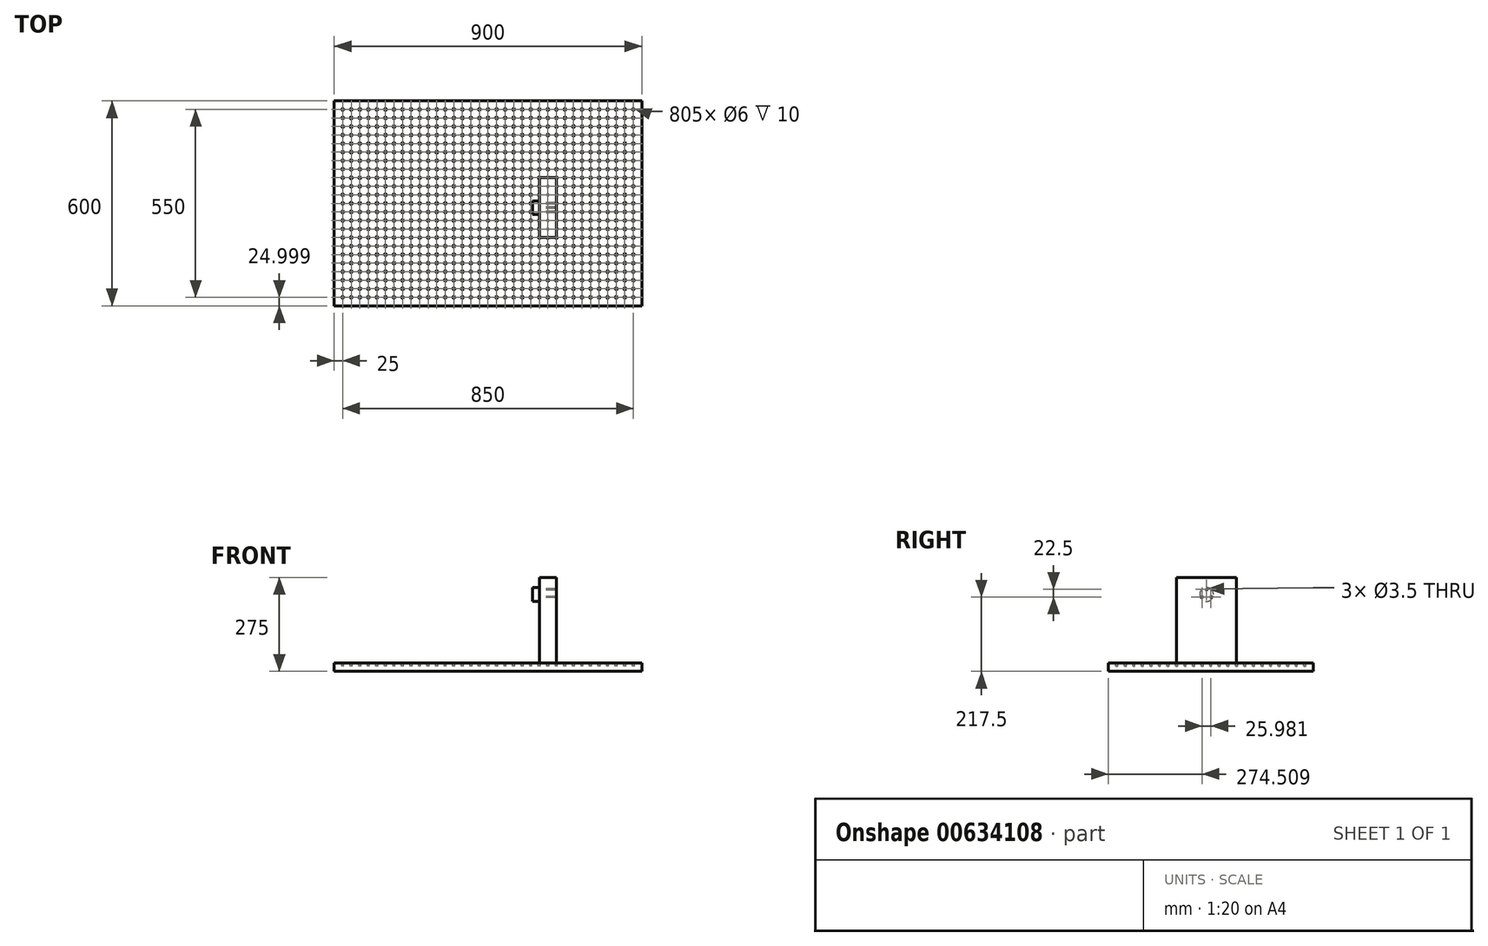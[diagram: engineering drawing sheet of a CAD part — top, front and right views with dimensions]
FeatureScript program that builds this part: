
annotation { "Feature Type Name" : "Feature", "Feature Type Description" : "" }
export const myFeature = defineFeature(function(context is Context, id is Id, definition is map)
    precondition{}
    {
        {
            var Q0;
            Q0=qCreatedBy(makeId("Top.planeOp"),FACE);
            var sketch = newSketch(context, id + "F0", { "sketchPlane" : qUnion([Q0])});
            skLineSegment(sketch, "E0.bottom", {"start": v(0, 7.98) * mm, "end": v(900, 7.98) * mm});
            skLineSegment(sketch, "E0.top", {"start": v(0, 607.98) * mm, "end": v(900, 607.98) * mm});
            skLineSegment(sketch, "E0.left", {"start": v(0, 7.98) * mm, "end": v(0, 607.98) * mm});
            skLineSegment(sketch, "E0.right", {"start": v(900, 7.98) * mm, "end": v(900, 607.98) * mm});
            skSolve(sketch);
        }
        {
            var Q0;
            Q0=makeQuery(id+"F0.imprint","IMPRINT",FACE,{"disambiguationData":[TD([[makeQuery(id+"F0.imprint","IMPRINT",EDGE,{"derivedFrom":sQuery(id+"F0.wireOp",EDGE,"E0.bottom")}),1.0]])]});
            extrude(context, id + "F1", {"entities" : qUnion([Q0]), "depth" : 25 * mm});
        }
        {
            var Q0;
            Q0=makeQuery(id+"F1.opExtrude","CAP_FACE",FACE,{"disambiguationData":[OSD([sQuery(id+"F0.wireOp",EDGE,"E0.bottom"),sQuery(id+"F0.wireOp",EDGE,"E0.top"),sQuery(id+"F0.wireOp",EDGE,"E0.left"),sQuery(id+"F0.wireOp",EDGE,"E0.right")])],"isStart":false});
            var sketch = newSketch(context, id + "F2", { "sketchPlane" : qUnion([Q0])});
            skCircle(sketch, "E1", {"center": v(25, 32.98) * mm, "radius": 3 * mm});
            skCircle(sketch, "E2.0.1.0", {"center": v(25, 57.98) * mm, "radius": 3 * mm});
            skCircle(sketch, "E2.0.2.0", {"center": v(25, 82.98) * mm, "radius": 3 * mm});
            skCircle(sketch, "E2.0.3.0", {"center": v(25, 107.98) * mm, "radius": 3 * mm});
            skCircle(sketch, "E2.0.4.0", {"center": v(25, 132.98) * mm, "radius": 3 * mm});
            skCircle(sketch, "E2.0.5.0", {"center": v(25, 157.98) * mm, "radius": 3 * mm});
            skCircle(sketch, "E2.0.6.0", {"center": v(25, 182.98) * mm, "radius": 3 * mm});
            skCircle(sketch, "E2.0.7.0", {"center": v(25, 207.98) * mm, "radius": 3 * mm});
            skCircle(sketch, "E2.0.8.0", {"center": v(25, 232.98) * mm, "radius": 3 * mm});
            skCircle(sketch, "E2.0.9.0", {"center": v(25, 257.98) * mm, "radius": 3 * mm});
            skCircle(sketch, "E2.0.10.0", {"center": v(25, 282.98) * mm, "radius": 3 * mm});
            skCircle(sketch, "E2.0.11.0", {"center": v(25, 307.98) * mm, "radius": 3 * mm});
            skCircle(sketch, "E2.0.12.0", {"center": v(25, 332.98) * mm, "radius": 3 * mm});
            skCircle(sketch, "E2.0.13.0", {"center": v(25, 357.98) * mm, "radius": 3 * mm});
            skCircle(sketch, "E2.0.14.0", {"center": v(25, 382.98) * mm, "radius": 3 * mm});
            skCircle(sketch, "E2.0.15.0", {"center": v(25, 407.98) * mm, "radius": 3 * mm});
            skCircle(sketch, "E2.0.16.0", {"center": v(25, 432.98) * mm, "radius": 3 * mm});
            skCircle(sketch, "E2.0.17.0", {"center": v(25, 457.98) * mm, "radius": 3 * mm});
            skCircle(sketch, "E2.0.18.0", {"center": v(25, 482.98) * mm, "radius": 3 * mm});
            skCircle(sketch, "E2.0.19.0", {"center": v(25, 507.98) * mm, "radius": 3 * mm});
            skCircle(sketch, "E2.0.20.0", {"center": v(25, 532.98) * mm, "radius": 3 * mm});
            skCircle(sketch, "E2.0.21.0", {"center": v(25, 557.98) * mm, "radius": 3 * mm});
            skCircle(sketch, "E2.0.22.0", {"center": v(25, 582.98) * mm, "radius": 3 * mm});
            skCircle(sketch, "E2.1.0.0", {"center": v(50, 32.98) * mm, "radius": 3 * mm});
            skCircle(sketch, "E2.1.1.0", {"center": v(50, 57.98) * mm, "radius": 3 * mm});
            skCircle(sketch, "E2.1.2.0", {"center": v(50, 82.98) * mm, "radius": 3 * mm});
            skCircle(sketch, "E2.1.3.0", {"center": v(50, 107.98) * mm, "radius": 3 * mm});
            skCircle(sketch, "E2.1.4.0", {"center": v(50, 132.98) * mm, "radius": 3 * mm});
            skCircle(sketch, "E2.1.5.0", {"center": v(50, 157.98) * mm, "radius": 3 * mm});
            skCircle(sketch, "E2.1.6.0", {"center": v(50, 182.98) * mm, "radius": 3 * mm});
            skCircle(sketch, "E2.1.7.0", {"center": v(50, 207.98) * mm, "radius": 3 * mm});
            skCircle(sketch, "E2.1.8.0", {"center": v(50, 232.98) * mm, "radius": 3 * mm});
            skCircle(sketch, "E2.1.9.0", {"center": v(50, 257.98) * mm, "radius": 3 * mm});
            skCircle(sketch, "E2.1.10.0", {"center": v(50, 282.98) * mm, "radius": 3 * mm});
            skCircle(sketch, "E2.1.11.0", {"center": v(50, 307.98) * mm, "radius": 3 * mm});
            skCircle(sketch, "E2.1.12.0", {"center": v(50, 332.98) * mm, "radius": 3 * mm});
            skCircle(sketch, "E2.1.13.0", {"center": v(50, 357.98) * mm, "radius": 3 * mm});
            skCircle(sketch, "E2.1.14.0", {"center": v(50, 382.98) * mm, "radius": 3 * mm});
            skCircle(sketch, "E2.1.15.0", {"center": v(50, 407.98) * mm, "radius": 3 * mm});
            skCircle(sketch, "E2.1.16.0", {"center": v(50, 432.98) * mm, "radius": 3 * mm});
            skCircle(sketch, "E2.1.17.0", {"center": v(50, 457.98) * mm, "radius": 3 * mm});
            skCircle(sketch, "E2.1.18.0", {"center": v(50, 482.98) * mm, "radius": 3 * mm});
            skCircle(sketch, "E2.1.19.0", {"center": v(50, 507.98) * mm, "radius": 3 * mm});
            skCircle(sketch, "E2.1.20.0", {"center": v(50, 532.98) * mm, "radius": 3 * mm});
            skCircle(sketch, "E2.1.21.0", {"center": v(50, 557.98) * mm, "radius": 3 * mm});
            skCircle(sketch, "E2.1.22.0", {"center": v(50, 582.98) * mm, "radius": 3 * mm});
            skCircle(sketch, "E2.2.0.0", {"center": v(75, 32.98) * mm, "radius": 3 * mm});
            skCircle(sketch, "E2.2.1.0", {"center": v(75, 57.98) * mm, "radius": 3 * mm});
            skCircle(sketch, "E2.2.2.0", {"center": v(75, 82.98) * mm, "radius": 3 * mm});
            skCircle(sketch, "E2.2.3.0", {"center": v(75, 107.98) * mm, "radius": 3 * mm});
            skCircle(sketch, "E2.2.4.0", {"center": v(75, 132.98) * mm, "radius": 3 * mm});
            skCircle(sketch, "E2.2.5.0", {"center": v(75, 157.98) * mm, "radius": 3 * mm});
            skCircle(sketch, "E2.2.6.0", {"center": v(75, 182.98) * mm, "radius": 3 * mm});
            skCircle(sketch, "E2.2.7.0", {"center": v(75, 207.98) * mm, "radius": 3 * mm});
            skCircle(sketch, "E2.2.8.0", {"center": v(75, 232.98) * mm, "radius": 3 * mm});
            skCircle(sketch, "E2.2.9.0", {"center": v(75, 257.98) * mm, "radius": 3 * mm});
            skCircle(sketch, "E2.2.10.0", {"center": v(75, 282.98) * mm, "radius": 3 * mm});
            skCircle(sketch, "E2.2.11.0", {"center": v(75, 307.98) * mm, "radius": 3 * mm});
            skCircle(sketch, "E2.2.12.0", {"center": v(75, 332.98) * mm, "radius": 3 * mm});
            skCircle(sketch, "E2.2.13.0", {"center": v(75, 357.98) * mm, "radius": 3 * mm});
            skCircle(sketch, "E2.2.14.0", {"center": v(75, 382.98) * mm, "radius": 3 * mm});
            skCircle(sketch, "E2.2.15.0", {"center": v(75, 407.98) * mm, "radius": 3 * mm});
            skCircle(sketch, "E2.2.16.0", {"center": v(75, 432.98) * mm, "radius": 3 * mm});
            skCircle(sketch, "E2.2.17.0", {"center": v(75, 457.98) * mm, "radius": 3 * mm});
            skCircle(sketch, "E2.2.18.0", {"center": v(75, 482.98) * mm, "radius": 3 * mm});
            skCircle(sketch, "E2.2.19.0", {"center": v(75, 507.98) * mm, "radius": 3 * mm});
            skCircle(sketch, "E2.2.20.0", {"center": v(75, 532.98) * mm, "radius": 3 * mm});
            skCircle(sketch, "E2.2.21.0", {"center": v(75, 557.98) * mm, "radius": 3 * mm});
            skCircle(sketch, "E2.2.22.0", {"center": v(75, 582.98) * mm, "radius": 3 * mm});
            skCircle(sketch, "E2.3.0.0", {"center": v(100, 32.98) * mm, "radius": 3 * mm});
            skCircle(sketch, "E2.3.1.0", {"center": v(100, 57.98) * mm, "radius": 3 * mm});
            skCircle(sketch, "E2.3.2.0", {"center": v(100, 82.98) * mm, "radius": 3 * mm});
            skCircle(sketch, "E2.3.3.0", {"center": v(100, 107.98) * mm, "radius": 3 * mm});
            skCircle(sketch, "E2.3.4.0", {"center": v(100, 132.98) * mm, "radius": 3 * mm});
            skCircle(sketch, "E2.3.5.0", {"center": v(100, 157.98) * mm, "radius": 3 * mm});
            skCircle(sketch, "E2.3.6.0", {"center": v(100, 182.98) * mm, "radius": 3 * mm});
            skCircle(sketch, "E2.3.7.0", {"center": v(100, 207.98) * mm, "radius": 3 * mm});
            skCircle(sketch, "E2.3.8.0", {"center": v(100, 232.98) * mm, "radius": 3 * mm});
            skCircle(sketch, "E2.3.9.0", {"center": v(100, 257.98) * mm, "radius": 3 * mm});
            skCircle(sketch, "E2.3.10.0", {"center": v(100, 282.98) * mm, "radius": 3 * mm});
            skCircle(sketch, "E2.3.11.0", {"center": v(100, 307.98) * mm, "radius": 3 * mm});
            skCircle(sketch, "E2.3.12.0", {"center": v(100, 332.98) * mm, "radius": 3 * mm});
            skCircle(sketch, "E2.3.13.0", {"center": v(100, 357.98) * mm, "radius": 3 * mm});
            skCircle(sketch, "E2.3.14.0", {"center": v(100, 382.98) * mm, "radius": 3 * mm});
            skCircle(sketch, "E2.3.15.0", {"center": v(100, 407.98) * mm, "radius": 3 * mm});
            skCircle(sketch, "E2.3.16.0", {"center": v(100, 432.98) * mm, "radius": 3 * mm});
            skCircle(sketch, "E2.3.17.0", {"center": v(100, 457.98) * mm, "radius": 3 * mm});
            skCircle(sketch, "E2.3.18.0", {"center": v(100, 482.98) * mm, "radius": 3 * mm});
            skCircle(sketch, "E2.3.19.0", {"center": v(100, 507.98) * mm, "radius": 3 * mm});
            skCircle(sketch, "E2.3.20.0", {"center": v(100, 532.98) * mm, "radius": 3 * mm});
            skCircle(sketch, "E2.3.21.0", {"center": v(100, 557.98) * mm, "radius": 3 * mm});
            skCircle(sketch, "E2.3.22.0", {"center": v(100, 582.98) * mm, "radius": 3 * mm});
            skCircle(sketch, "E2.4.0.0", {"center": v(125, 32.98) * mm, "radius": 3 * mm});
            skCircle(sketch, "E2.4.1.0", {"center": v(125, 57.98) * mm, "radius": 3 * mm});
            skCircle(sketch, "E2.4.2.0", {"center": v(125, 82.98) * mm, "radius": 3 * mm});
            skCircle(sketch, "E2.4.3.0", {"center": v(125, 107.98) * mm, "radius": 3 * mm});
            skCircle(sketch, "E2.4.4.0", {"center": v(125, 132.98) * mm, "radius": 3 * mm});
            skCircle(sketch, "E2.4.5.0", {"center": v(125, 157.98) * mm, "radius": 3 * mm});
            skCircle(sketch, "E2.4.6.0", {"center": v(125, 182.98) * mm, "radius": 3 * mm});
            skCircle(sketch, "E2.4.7.0", {"center": v(125, 207.98) * mm, "radius": 3 * mm});
            skCircle(sketch, "E2.4.8.0", {"center": v(125, 232.98) * mm, "radius": 3 * mm});
            skCircle(sketch, "E2.4.9.0", {"center": v(125, 257.98) * mm, "radius": 3 * mm});
            skCircle(sketch, "E2.4.10.0", {"center": v(125, 282.98) * mm, "radius": 3 * mm});
            skCircle(sketch, "E2.4.11.0", {"center": v(125, 307.98) * mm, "radius": 3 * mm});
            skCircle(sketch, "E2.4.12.0", {"center": v(125, 332.98) * mm, "radius": 3 * mm});
            skCircle(sketch, "E2.4.13.0", {"center": v(125, 357.98) * mm, "radius": 3 * mm});
            skCircle(sketch, "E2.4.14.0", {"center": v(125, 382.98) * mm, "radius": 3 * mm});
            skCircle(sketch, "E2.4.15.0", {"center": v(125, 407.98) * mm, "radius": 3 * mm});
            skCircle(sketch, "E2.4.16.0", {"center": v(125, 432.98) * mm, "radius": 3 * mm});
            skCircle(sketch, "E2.4.17.0", {"center": v(125, 457.98) * mm, "radius": 3 * mm});
            skCircle(sketch, "E2.4.18.0", {"center": v(125, 482.98) * mm, "radius": 3 * mm});
            skCircle(sketch, "E2.4.19.0", {"center": v(125, 507.98) * mm, "radius": 3 * mm});
            skCircle(sketch, "E2.4.20.0", {"center": v(125, 532.98) * mm, "radius": 3 * mm});
            skCircle(sketch, "E2.4.21.0", {"center": v(125, 557.98) * mm, "radius": 3 * mm});
            skCircle(sketch, "E2.4.22.0", {"center": v(125, 582.98) * mm, "radius": 3 * mm});
            skCircle(sketch, "E2.5.0.0", {"center": v(150, 32.98) * mm, "radius": 3 * mm});
            skCircle(sketch, "E2.5.1.0", {"center": v(150, 57.98) * mm, "radius": 3 * mm});
            skCircle(sketch, "E2.5.2.0", {"center": v(150, 82.98) * mm, "radius": 3 * mm});
            skCircle(sketch, "E2.5.3.0", {"center": v(150, 107.98) * mm, "radius": 3 * mm});
            skCircle(sketch, "E2.5.4.0", {"center": v(150, 132.98) * mm, "radius": 3 * mm});
            skCircle(sketch, "E2.5.5.0", {"center": v(150, 157.98) * mm, "radius": 3 * mm});
            skCircle(sketch, "E2.5.6.0", {"center": v(150, 182.98) * mm, "radius": 3 * mm});
            skCircle(sketch, "E2.5.7.0", {"center": v(150, 207.98) * mm, "radius": 3 * mm});
            skCircle(sketch, "E2.5.8.0", {"center": v(150, 232.98) * mm, "radius": 3 * mm});
            skCircle(sketch, "E2.5.9.0", {"center": v(150, 257.98) * mm, "radius": 3 * mm});
            skCircle(sketch, "E2.5.10.0", {"center": v(150, 282.98) * mm, "radius": 3 * mm});
            skCircle(sketch, "E2.5.11.0", {"center": v(150, 307.98) * mm, "radius": 3 * mm});
            skCircle(sketch, "E2.5.12.0", {"center": v(150, 332.98) * mm, "radius": 3 * mm});
            skCircle(sketch, "E2.5.13.0", {"center": v(150, 357.98) * mm, "radius": 3 * mm});
            skCircle(sketch, "E2.5.14.0", {"center": v(150, 382.98) * mm, "radius": 3 * mm});
            skCircle(sketch, "E2.5.15.0", {"center": v(150, 407.98) * mm, "radius": 3 * mm});
            skCircle(sketch, "E2.5.16.0", {"center": v(150, 432.98) * mm, "radius": 3 * mm});
            skCircle(sketch, "E2.5.17.0", {"center": v(150, 457.98) * mm, "radius": 3 * mm});
            skCircle(sketch, "E2.5.18.0", {"center": v(150, 482.98) * mm, "radius": 3 * mm});
            skCircle(sketch, "E2.5.19.0", {"center": v(150, 507.98) * mm, "radius": 3 * mm});
            skCircle(sketch, "E2.5.20.0", {"center": v(150, 532.98) * mm, "radius": 3 * mm});
            skCircle(sketch, "E2.5.21.0", {"center": v(150, 557.98) * mm, "radius": 3 * mm});
            skCircle(sketch, "E2.5.22.0", {"center": v(150, 582.98) * mm, "radius": 3 * mm});
            skCircle(sketch, "E2.6.0.0", {"center": v(175, 32.98) * mm, "radius": 3 * mm});
            skCircle(sketch, "E2.6.1.0", {"center": v(175, 57.98) * mm, "radius": 3 * mm});
            skCircle(sketch, "E2.6.2.0", {"center": v(175, 82.98) * mm, "radius": 3 * mm});
            skCircle(sketch, "E2.6.3.0", {"center": v(175, 107.98) * mm, "radius": 3 * mm});
            skCircle(sketch, "E2.6.4.0", {"center": v(175, 132.98) * mm, "radius": 3 * mm});
            skCircle(sketch, "E2.6.5.0", {"center": v(175, 157.98) * mm, "radius": 3 * mm});
            skCircle(sketch, "E2.6.6.0", {"center": v(175, 182.98) * mm, "radius": 3 * mm});
            skCircle(sketch, "E2.6.7.0", {"center": v(175, 207.98) * mm, "radius": 3 * mm});
            skCircle(sketch, "E2.6.8.0", {"center": v(175, 232.98) * mm, "radius": 3 * mm});
            skCircle(sketch, "E2.6.9.0", {"center": v(175, 257.98) * mm, "radius": 3 * mm});
            skCircle(sketch, "E2.6.10.0", {"center": v(175, 282.98) * mm, "radius": 3 * mm});
            skCircle(sketch, "E2.6.11.0", {"center": v(175, 307.98) * mm, "radius": 3 * mm});
            skCircle(sketch, "E2.6.12.0", {"center": v(175, 332.98) * mm, "radius": 3 * mm});
            skCircle(sketch, "E2.6.13.0", {"center": v(175, 357.98) * mm, "radius": 3 * mm});
            skCircle(sketch, "E2.6.14.0", {"center": v(175, 382.98) * mm, "radius": 3 * mm});
            skCircle(sketch, "E2.6.15.0", {"center": v(175, 407.98) * mm, "radius": 3 * mm});
            skCircle(sketch, "E2.6.16.0", {"center": v(175, 432.98) * mm, "radius": 3 * mm});
            skCircle(sketch, "E2.6.17.0", {"center": v(175, 457.98) * mm, "radius": 3 * mm});
            skCircle(sketch, "E2.6.18.0", {"center": v(175, 482.98) * mm, "radius": 3 * mm});
            skCircle(sketch, "E2.6.19.0", {"center": v(175, 507.98) * mm, "radius": 3 * mm});
            skCircle(sketch, "E2.6.20.0", {"center": v(175, 532.98) * mm, "radius": 3 * mm});
            skCircle(sketch, "E2.6.21.0", {"center": v(175, 557.98) * mm, "radius": 3 * mm});
            skCircle(sketch, "E2.6.22.0", {"center": v(175, 582.98) * mm, "radius": 3 * mm});
            skCircle(sketch, "E2.7.0.0", {"center": v(200, 32.98) * mm, "radius": 3 * mm});
            skCircle(sketch, "E2.7.1.0", {"center": v(200, 57.98) * mm, "radius": 3 * mm});
            skCircle(sketch, "E2.7.2.0", {"center": v(200, 82.98) * mm, "radius": 3 * mm});
            skCircle(sketch, "E2.7.3.0", {"center": v(200, 107.98) * mm, "radius": 3 * mm});
            skCircle(sketch, "E2.7.4.0", {"center": v(200, 132.98) * mm, "radius": 3 * mm});
            skCircle(sketch, "E2.7.5.0", {"center": v(200, 157.98) * mm, "radius": 3 * mm});
            skCircle(sketch, "E2.7.6.0", {"center": v(200, 182.98) * mm, "radius": 3 * mm});
            skCircle(sketch, "E2.7.7.0", {"center": v(200, 207.98) * mm, "radius": 3 * mm});
            skCircle(sketch, "E2.7.8.0", {"center": v(200, 232.98) * mm, "radius": 3 * mm});
            skCircle(sketch, "E2.7.9.0", {"center": v(200, 257.98) * mm, "radius": 3 * mm});
            skCircle(sketch, "E2.7.10.0", {"center": v(200, 282.98) * mm, "radius": 3 * mm});
            skCircle(sketch, "E2.7.11.0", {"center": v(200, 307.98) * mm, "radius": 3 * mm});
            skCircle(sketch, "E2.7.12.0", {"center": v(200, 332.98) * mm, "radius": 3 * mm});
            skCircle(sketch, "E2.7.13.0", {"center": v(200, 357.98) * mm, "radius": 3 * mm});
            skCircle(sketch, "E2.7.14.0", {"center": v(200, 382.98) * mm, "radius": 3 * mm});
            skCircle(sketch, "E2.7.15.0", {"center": v(200, 407.98) * mm, "radius": 3 * mm});
            skCircle(sketch, "E2.7.16.0", {"center": v(200, 432.98) * mm, "radius": 3 * mm});
            skCircle(sketch, "E2.7.17.0", {"center": v(200, 457.98) * mm, "radius": 3 * mm});
            skCircle(sketch, "E2.7.18.0", {"center": v(200, 482.98) * mm, "radius": 3 * mm});
            skCircle(sketch, "E2.7.19.0", {"center": v(200, 507.98) * mm, "radius": 3 * mm});
            skCircle(sketch, "E2.7.20.0", {"center": v(200, 532.98) * mm, "radius": 3 * mm});
            skCircle(sketch, "E2.7.21.0", {"center": v(200, 557.98) * mm, "radius": 3 * mm});
            skCircle(sketch, "E2.7.22.0", {"center": v(200, 582.98) * mm, "radius": 3 * mm});
            skCircle(sketch, "E2.8.0.0", {"center": v(225, 32.98) * mm, "radius": 3 * mm});
            skCircle(sketch, "E2.8.1.0", {"center": v(225, 57.98) * mm, "radius": 3 * mm});
            skCircle(sketch, "E2.8.2.0", {"center": v(225, 82.98) * mm, "radius": 3 * mm});
            skCircle(sketch, "E2.8.3.0", {"center": v(225, 107.98) * mm, "radius": 3 * mm});
            skCircle(sketch, "E2.8.4.0", {"center": v(225, 132.98) * mm, "radius": 3 * mm});
            skCircle(sketch, "E2.8.5.0", {"center": v(225, 157.98) * mm, "radius": 3 * mm});
            skCircle(sketch, "E2.8.6.0", {"center": v(225, 182.98) * mm, "radius": 3 * mm});
            skCircle(sketch, "E2.8.7.0", {"center": v(225, 207.98) * mm, "radius": 3 * mm});
            skCircle(sketch, "E2.8.8.0", {"center": v(225, 232.98) * mm, "radius": 3 * mm});
            skCircle(sketch, "E2.8.9.0", {"center": v(225, 257.98) * mm, "radius": 3 * mm});
            skCircle(sketch, "E2.8.10.0", {"center": v(225, 282.98) * mm, "radius": 3 * mm});
            skCircle(sketch, "E2.8.11.0", {"center": v(225, 307.98) * mm, "radius": 3 * mm});
            skCircle(sketch, "E2.8.12.0", {"center": v(225, 332.98) * mm, "radius": 3 * mm});
            skCircle(sketch, "E2.8.13.0", {"center": v(225, 357.98) * mm, "radius": 3 * mm});
            skCircle(sketch, "E2.8.14.0", {"center": v(225, 382.98) * mm, "radius": 3 * mm});
            skCircle(sketch, "E2.8.15.0", {"center": v(225, 407.98) * mm, "radius": 3 * mm});
            skCircle(sketch, "E2.8.16.0", {"center": v(225, 432.98) * mm, "radius": 3 * mm});
            skCircle(sketch, "E2.8.17.0", {"center": v(225, 457.98) * mm, "radius": 3 * mm});
            skCircle(sketch, "E2.8.18.0", {"center": v(225, 482.98) * mm, "radius": 3 * mm});
            skCircle(sketch, "E2.8.19.0", {"center": v(225, 507.98) * mm, "radius": 3 * mm});
            skCircle(sketch, "E2.8.20.0", {"center": v(225, 532.98) * mm, "radius": 3 * mm});
            skCircle(sketch, "E2.8.21.0", {"center": v(225, 557.98) * mm, "radius": 3 * mm});
            skCircle(sketch, "E2.8.22.0", {"center": v(225, 582.98) * mm, "radius": 3 * mm});
            skCircle(sketch, "E2.9.0.0", {"center": v(250, 32.98) * mm, "radius": 3 * mm});
            skCircle(sketch, "E2.9.1.0", {"center": v(250, 57.98) * mm, "radius": 3 * mm});
            skCircle(sketch, "E2.9.2.0", {"center": v(250, 82.98) * mm, "radius": 3 * mm});
            skCircle(sketch, "E2.9.3.0", {"center": v(250, 107.98) * mm, "radius": 3 * mm});
            skCircle(sketch, "E2.9.4.0", {"center": v(250, 132.98) * mm, "radius": 3 * mm});
            skCircle(sketch, "E2.9.5.0", {"center": v(250, 157.98) * mm, "radius": 3 * mm});
            skCircle(sketch, "E2.9.6.0", {"center": v(250, 182.98) * mm, "radius": 3 * mm});
            skCircle(sketch, "E2.9.7.0", {"center": v(250, 207.98) * mm, "radius": 3 * mm});
            skCircle(sketch, "E2.9.8.0", {"center": v(250, 232.98) * mm, "radius": 3 * mm});
            skCircle(sketch, "E2.9.9.0", {"center": v(250, 257.98) * mm, "radius": 3 * mm});
            skCircle(sketch, "E2.9.10.0", {"center": v(250, 282.98) * mm, "radius": 3 * mm});
            skCircle(sketch, "E2.9.11.0", {"center": v(250, 307.98) * mm, "radius": 3 * mm});
            skCircle(sketch, "E2.9.12.0", {"center": v(250, 332.98) * mm, "radius": 3 * mm});
            skCircle(sketch, "E2.9.13.0", {"center": v(250, 357.98) * mm, "radius": 3 * mm});
            skCircle(sketch, "E2.9.14.0", {"center": v(250, 382.98) * mm, "radius": 3 * mm});
            skCircle(sketch, "E2.9.15.0", {"center": v(250, 407.98) * mm, "radius": 3 * mm});
            skCircle(sketch, "E2.9.16.0", {"center": v(250, 432.98) * mm, "radius": 3 * mm});
            skCircle(sketch, "E2.9.17.0", {"center": v(250, 457.98) * mm, "radius": 3 * mm});
            skCircle(sketch, "E2.9.18.0", {"center": v(250, 482.98) * mm, "radius": 3 * mm});
            skCircle(sketch, "E2.9.19.0", {"center": v(250, 507.98) * mm, "radius": 3 * mm});
            skCircle(sketch, "E2.9.20.0", {"center": v(250, 532.98) * mm, "radius": 3 * mm});
            skCircle(sketch, "E2.9.21.0", {"center": v(250, 557.98) * mm, "radius": 3 * mm});
            skCircle(sketch, "E2.9.22.0", {"center": v(250, 582.98) * mm, "radius": 3 * mm});
            skCircle(sketch, "E2.10.0.0", {"center": v(275, 32.98) * mm, "radius": 3 * mm});
            skCircle(sketch, "E2.10.1.0", {"center": v(275, 57.98) * mm, "radius": 3 * mm});
            skCircle(sketch, "E2.10.2.0", {"center": v(275, 82.98) * mm, "radius": 3 * mm});
            skCircle(sketch, "E2.10.3.0", {"center": v(275, 107.98) * mm, "radius": 3 * mm});
            skCircle(sketch, "E2.10.4.0", {"center": v(275, 132.98) * mm, "radius": 3 * mm});
            skCircle(sketch, "E2.10.5.0", {"center": v(275, 157.98) * mm, "radius": 3 * mm});
            skCircle(sketch, "E2.10.6.0", {"center": v(275, 182.98) * mm, "radius": 3 * mm});
            skCircle(sketch, "E2.10.7.0", {"center": v(275, 207.98) * mm, "radius": 3 * mm});
            skCircle(sketch, "E2.10.8.0", {"center": v(275, 232.98) * mm, "radius": 3 * mm});
            skCircle(sketch, "E2.10.9.0", {"center": v(275, 257.98) * mm, "radius": 3 * mm});
            skCircle(sketch, "E2.10.10.0", {"center": v(275, 282.98) * mm, "radius": 3 * mm});
            skCircle(sketch, "E2.10.11.0", {"center": v(275, 307.98) * mm, "radius": 3 * mm});
            skCircle(sketch, "E2.10.12.0", {"center": v(275, 332.98) * mm, "radius": 3 * mm});
            skCircle(sketch, "E2.10.13.0", {"center": v(275, 357.98) * mm, "radius": 3 * mm});
            skCircle(sketch, "E2.10.14.0", {"center": v(275, 382.98) * mm, "radius": 3 * mm});
            skCircle(sketch, "E2.10.15.0", {"center": v(275, 407.98) * mm, "radius": 3 * mm});
            skCircle(sketch, "E2.10.16.0", {"center": v(275, 432.98) * mm, "radius": 3 * mm});
            skCircle(sketch, "E2.10.17.0", {"center": v(275, 457.98) * mm, "radius": 3 * mm});
            skCircle(sketch, "E2.10.18.0", {"center": v(275, 482.98) * mm, "radius": 3 * mm});
            skCircle(sketch, "E2.10.19.0", {"center": v(275, 507.98) * mm, "radius": 3 * mm});
            skCircle(sketch, "E2.10.20.0", {"center": v(275, 532.98) * mm, "radius": 3 * mm});
            skCircle(sketch, "E2.10.21.0", {"center": v(275, 557.98) * mm, "radius": 3 * mm});
            skCircle(sketch, "E2.10.22.0", {"center": v(275, 582.98) * mm, "radius": 3 * mm});
            skCircle(sketch, "E2.11.0.0", {"center": v(300, 32.98) * mm, "radius": 3 * mm});
            skCircle(sketch, "E2.11.1.0", {"center": v(300, 57.98) * mm, "radius": 3 * mm});
            skCircle(sketch, "E2.11.2.0", {"center": v(300, 82.98) * mm, "radius": 3 * mm});
            skCircle(sketch, "E2.11.3.0", {"center": v(300, 107.98) * mm, "radius": 3 * mm});
            skCircle(sketch, "E2.11.4.0", {"center": v(300, 132.98) * mm, "radius": 3 * mm});
            skCircle(sketch, "E2.11.5.0", {"center": v(300, 157.98) * mm, "radius": 3 * mm});
            skCircle(sketch, "E2.11.6.0", {"center": v(300, 182.98) * mm, "radius": 3 * mm});
            skCircle(sketch, "E2.11.7.0", {"center": v(300, 207.98) * mm, "radius": 3 * mm});
            skCircle(sketch, "E2.11.8.0", {"center": v(300, 232.98) * mm, "radius": 3 * mm});
            skCircle(sketch, "E2.11.9.0", {"center": v(300, 257.98) * mm, "radius": 3 * mm});
            skCircle(sketch, "E2.11.10.0", {"center": v(300, 282.98) * mm, "radius": 3 * mm});
            skCircle(sketch, "E2.11.11.0", {"center": v(300, 307.98) * mm, "radius": 3 * mm});
            skCircle(sketch, "E2.11.12.0", {"center": v(300, 332.98) * mm, "radius": 3 * mm});
            skCircle(sketch, "E2.11.13.0", {"center": v(300, 357.98) * mm, "radius": 3 * mm});
            skCircle(sketch, "E2.11.14.0", {"center": v(300, 382.98) * mm, "radius": 3 * mm});
            skCircle(sketch, "E2.11.15.0", {"center": v(300, 407.98) * mm, "radius": 3 * mm});
            skCircle(sketch, "E2.11.16.0", {"center": v(300, 432.98) * mm, "radius": 3 * mm});
            skCircle(sketch, "E2.11.17.0", {"center": v(300, 457.98) * mm, "radius": 3 * mm});
            skCircle(sketch, "E2.11.18.0", {"center": v(300, 482.98) * mm, "radius": 3 * mm});
            skCircle(sketch, "E2.11.19.0", {"center": v(300, 507.98) * mm, "radius": 3 * mm});
            skCircle(sketch, "E2.11.20.0", {"center": v(300, 532.98) * mm, "radius": 3 * mm});
            skCircle(sketch, "E2.11.21.0", {"center": v(300, 557.98) * mm, "radius": 3 * mm});
            skCircle(sketch, "E2.11.22.0", {"center": v(300, 582.98) * mm, "radius": 3 * mm});
            skCircle(sketch, "E2.12.0.0", {"center": v(325, 32.98) * mm, "radius": 3 * mm});
            skCircle(sketch, "E2.12.1.0", {"center": v(325, 57.98) * mm, "radius": 3 * mm});
            skCircle(sketch, "E2.12.2.0", {"center": v(325, 82.98) * mm, "radius": 3 * mm});
            skCircle(sketch, "E2.12.3.0", {"center": v(325, 107.98) * mm, "radius": 3 * mm});
            skCircle(sketch, "E2.12.4.0", {"center": v(325, 132.98) * mm, "radius": 3 * mm});
            skCircle(sketch, "E2.12.5.0", {"center": v(325, 157.98) * mm, "radius": 3 * mm});
            skCircle(sketch, "E2.12.6.0", {"center": v(325, 182.98) * mm, "radius": 3 * mm});
            skCircle(sketch, "E2.12.7.0", {"center": v(325, 207.98) * mm, "radius": 3 * mm});
            skCircle(sketch, "E2.12.8.0", {"center": v(325, 232.98) * mm, "radius": 3 * mm});
            skCircle(sketch, "E2.12.9.0", {"center": v(325, 257.98) * mm, "radius": 3 * mm});
            skCircle(sketch, "E2.12.10.0", {"center": v(325, 282.98) * mm, "radius": 3 * mm});
            skCircle(sketch, "E2.12.11.0", {"center": v(325, 307.98) * mm, "radius": 3 * mm});
            skCircle(sketch, "E2.12.12.0", {"center": v(325, 332.98) * mm, "radius": 3 * mm});
            skCircle(sketch, "E2.12.13.0", {"center": v(325, 357.98) * mm, "radius": 3 * mm});
            skCircle(sketch, "E2.12.14.0", {"center": v(325, 382.98) * mm, "radius": 3 * mm});
            skCircle(sketch, "E2.12.15.0", {"center": v(325, 407.98) * mm, "radius": 3 * mm});
            skCircle(sketch, "E2.12.16.0", {"center": v(325, 432.98) * mm, "radius": 3 * mm});
            skCircle(sketch, "E2.12.17.0", {"center": v(325, 457.98) * mm, "radius": 3 * mm});
            skCircle(sketch, "E2.12.18.0", {"center": v(325, 482.98) * mm, "radius": 3 * mm});
            skCircle(sketch, "E2.12.19.0", {"center": v(325, 507.98) * mm, "radius": 3 * mm});
            skCircle(sketch, "E2.12.20.0", {"center": v(325, 532.98) * mm, "radius": 3 * mm});
            skCircle(sketch, "E2.12.21.0", {"center": v(325, 557.98) * mm, "radius": 3 * mm});
            skCircle(sketch, "E2.12.22.0", {"center": v(325, 582.98) * mm, "radius": 3 * mm});
            skCircle(sketch, "E2.13.0.0", {"center": v(350, 32.98) * mm, "radius": 3 * mm});
            skCircle(sketch, "E2.13.1.0", {"center": v(350, 57.98) * mm, "radius": 3 * mm});
            skCircle(sketch, "E2.13.2.0", {"center": v(350, 82.98) * mm, "radius": 3 * mm});
            skCircle(sketch, "E2.13.3.0", {"center": v(350, 107.98) * mm, "radius": 3 * mm});
            skCircle(sketch, "E2.13.4.0", {"center": v(350, 132.98) * mm, "radius": 3 * mm});
            skCircle(sketch, "E2.13.5.0", {"center": v(350, 157.98) * mm, "radius": 3 * mm});
            skCircle(sketch, "E2.13.6.0", {"center": v(350, 182.98) * mm, "radius": 3 * mm});
            skCircle(sketch, "E2.13.7.0", {"center": v(350, 207.98) * mm, "radius": 3 * mm});
            skCircle(sketch, "E2.13.8.0", {"center": v(350, 232.98) * mm, "radius": 3 * mm});
            skCircle(sketch, "E2.13.9.0", {"center": v(350, 257.98) * mm, "radius": 3 * mm});
            skCircle(sketch, "E2.13.10.0", {"center": v(350, 282.98) * mm, "radius": 3 * mm});
            skCircle(sketch, "E2.13.11.0", {"center": v(350, 307.98) * mm, "radius": 3 * mm});
            skCircle(sketch, "E2.13.12.0", {"center": v(350, 332.98) * mm, "radius": 3 * mm});
            skCircle(sketch, "E2.13.13.0", {"center": v(350, 357.98) * mm, "radius": 3 * mm});
            skCircle(sketch, "E2.13.14.0", {"center": v(350, 382.98) * mm, "radius": 3 * mm});
            skCircle(sketch, "E2.13.15.0", {"center": v(350, 407.98) * mm, "radius": 3 * mm});
            skCircle(sketch, "E2.13.16.0", {"center": v(350, 432.98) * mm, "radius": 3 * mm});
            skCircle(sketch, "E2.13.17.0", {"center": v(350, 457.98) * mm, "radius": 3 * mm});
            skCircle(sketch, "E2.13.18.0", {"center": v(350, 482.98) * mm, "radius": 3 * mm});
            skCircle(sketch, "E2.13.19.0", {"center": v(350, 507.98) * mm, "radius": 3 * mm});
            skCircle(sketch, "E2.13.20.0", {"center": v(350, 532.98) * mm, "radius": 3 * mm});
            skCircle(sketch, "E2.13.21.0", {"center": v(350, 557.98) * mm, "radius": 3 * mm});
            skCircle(sketch, "E2.13.22.0", {"center": v(350, 582.98) * mm, "radius": 3 * mm});
            skCircle(sketch, "E2.14.0.0", {"center": v(375, 32.98) * mm, "radius": 3 * mm});
            skCircle(sketch, "E2.14.1.0", {"center": v(375, 57.98) * mm, "radius": 3 * mm});
            skCircle(sketch, "E2.14.2.0", {"center": v(375, 82.98) * mm, "radius": 3 * mm});
            skCircle(sketch, "E2.14.3.0", {"center": v(375, 107.98) * mm, "radius": 3 * mm});
            skCircle(sketch, "E2.14.4.0", {"center": v(375, 132.98) * mm, "radius": 3 * mm});
            skCircle(sketch, "E2.14.5.0", {"center": v(375, 157.98) * mm, "radius": 3 * mm});
            skCircle(sketch, "E2.14.6.0", {"center": v(375, 182.98) * mm, "radius": 3 * mm});
            skCircle(sketch, "E2.14.7.0", {"center": v(375, 207.98) * mm, "radius": 3 * mm});
            skCircle(sketch, "E2.14.8.0", {"center": v(375, 232.98) * mm, "radius": 3 * mm});
            skCircle(sketch, "E2.14.9.0", {"center": v(375, 257.98) * mm, "radius": 3 * mm});
            skCircle(sketch, "E2.14.10.0", {"center": v(375, 282.98) * mm, "radius": 3 * mm});
            skCircle(sketch, "E2.14.11.0", {"center": v(375, 307.98) * mm, "radius": 3 * mm});
            skCircle(sketch, "E2.14.12.0", {"center": v(375, 332.98) * mm, "radius": 3 * mm});
            skCircle(sketch, "E2.14.13.0", {"center": v(375, 357.98) * mm, "radius": 3 * mm});
            skCircle(sketch, "E2.14.14.0", {"center": v(375, 382.98) * mm, "radius": 3 * mm});
            skCircle(sketch, "E2.14.15.0", {"center": v(375, 407.98) * mm, "radius": 3 * mm});
            skCircle(sketch, "E2.14.16.0", {"center": v(375, 432.98) * mm, "radius": 3 * mm});
            skCircle(sketch, "E2.14.17.0", {"center": v(375, 457.98) * mm, "radius": 3 * mm});
            skCircle(sketch, "E2.14.18.0", {"center": v(375, 482.98) * mm, "radius": 3 * mm});
            skCircle(sketch, "E2.14.19.0", {"center": v(375, 507.98) * mm, "radius": 3 * mm});
            skCircle(sketch, "E2.14.20.0", {"center": v(375, 532.98) * mm, "radius": 3 * mm});
            skCircle(sketch, "E2.14.21.0", {"center": v(375, 557.98) * mm, "radius": 3 * mm});
            skCircle(sketch, "E2.14.22.0", {"center": v(375, 582.98) * mm, "radius": 3 * mm});
            skCircle(sketch, "E2.15.0.0", {"center": v(400, 32.98) * mm, "radius": 3 * mm});
            skCircle(sketch, "E2.15.1.0", {"center": v(400, 57.98) * mm, "radius": 3 * mm});
            skCircle(sketch, "E2.15.2.0", {"center": v(400, 82.98) * mm, "radius": 3 * mm});
            skCircle(sketch, "E2.15.3.0", {"center": v(400, 107.98) * mm, "radius": 3 * mm});
            skCircle(sketch, "E2.15.4.0", {"center": v(400, 132.98) * mm, "radius": 3 * mm});
            skCircle(sketch, "E2.15.5.0", {"center": v(400, 157.98) * mm, "radius": 3 * mm});
            skCircle(sketch, "E2.15.6.0", {"center": v(400, 182.98) * mm, "radius": 3 * mm});
            skCircle(sketch, "E2.15.7.0", {"center": v(400, 207.98) * mm, "radius": 3 * mm});
            skCircle(sketch, "E2.15.8.0", {"center": v(400, 232.98) * mm, "radius": 3 * mm});
            skCircle(sketch, "E2.15.9.0", {"center": v(400, 257.98) * mm, "radius": 3 * mm});
            skCircle(sketch, "E2.15.10.0", {"center": v(400, 282.98) * mm, "radius": 3 * mm});
            skCircle(sketch, "E2.15.11.0", {"center": v(400, 307.98) * mm, "radius": 3 * mm});
            skCircle(sketch, "E2.15.12.0", {"center": v(400, 332.98) * mm, "radius": 3 * mm});
            skCircle(sketch, "E2.15.13.0", {"center": v(400, 357.98) * mm, "radius": 3 * mm});
            skCircle(sketch, "E2.15.14.0", {"center": v(400, 382.98) * mm, "radius": 3 * mm});
            skCircle(sketch, "E2.15.15.0", {"center": v(400, 407.98) * mm, "radius": 3 * mm});
            skCircle(sketch, "E2.15.16.0", {"center": v(400, 432.98) * mm, "radius": 3 * mm});
            skCircle(sketch, "E2.15.17.0", {"center": v(400, 457.98) * mm, "radius": 3 * mm});
            skCircle(sketch, "E2.15.18.0", {"center": v(400, 482.98) * mm, "radius": 3 * mm});
            skCircle(sketch, "E2.15.19.0", {"center": v(400, 507.98) * mm, "radius": 3 * mm});
            skCircle(sketch, "E2.15.20.0", {"center": v(400, 532.98) * mm, "radius": 3 * mm});
            skCircle(sketch, "E2.15.21.0", {"center": v(400, 557.98) * mm, "radius": 3 * mm});
            skCircle(sketch, "E2.15.22.0", {"center": v(400, 582.98) * mm, "radius": 3 * mm});
            skCircle(sketch, "E2.16.0.0", {"center": v(425, 32.98) * mm, "radius": 3 * mm});
            skCircle(sketch, "E2.16.1.0", {"center": v(425, 57.98) * mm, "radius": 3 * mm});
            skCircle(sketch, "E2.16.2.0", {"center": v(425, 82.98) * mm, "radius": 3 * mm});
            skCircle(sketch, "E2.16.3.0", {"center": v(425, 107.98) * mm, "radius": 3 * mm});
            skCircle(sketch, "E2.16.4.0", {"center": v(425, 132.98) * mm, "radius": 3 * mm});
            skCircle(sketch, "E2.16.5.0", {"center": v(425, 157.98) * mm, "radius": 3 * mm});
            skCircle(sketch, "E2.16.6.0", {"center": v(425, 182.98) * mm, "radius": 3 * mm});
            skCircle(sketch, "E2.16.7.0", {"center": v(425, 207.98) * mm, "radius": 3 * mm});
            skCircle(sketch, "E2.16.8.0", {"center": v(425, 232.98) * mm, "radius": 3 * mm});
            skCircle(sketch, "E2.16.9.0", {"center": v(425, 257.98) * mm, "radius": 3 * mm});
            skCircle(sketch, "E2.16.10.0", {"center": v(425, 282.98) * mm, "radius": 3 * mm});
            skCircle(sketch, "E2.16.11.0", {"center": v(425, 307.98) * mm, "radius": 3 * mm});
            skCircle(sketch, "E2.16.12.0", {"center": v(425, 332.98) * mm, "radius": 3 * mm});
            skCircle(sketch, "E2.16.13.0", {"center": v(425, 357.98) * mm, "radius": 3 * mm});
            skCircle(sketch, "E2.16.14.0", {"center": v(425, 382.98) * mm, "radius": 3 * mm});
            skCircle(sketch, "E2.16.15.0", {"center": v(425, 407.98) * mm, "radius": 3 * mm});
            skCircle(sketch, "E2.16.16.0", {"center": v(425, 432.98) * mm, "radius": 3 * mm});
            skCircle(sketch, "E2.16.17.0", {"center": v(425, 457.98) * mm, "radius": 3 * mm});
            skCircle(sketch, "E2.16.18.0", {"center": v(425, 482.98) * mm, "radius": 3 * mm});
            skCircle(sketch, "E2.16.19.0", {"center": v(425, 507.98) * mm, "radius": 3 * mm});
            skCircle(sketch, "E2.16.20.0", {"center": v(425, 532.98) * mm, "radius": 3 * mm});
            skCircle(sketch, "E2.16.21.0", {"center": v(425, 557.98) * mm, "radius": 3 * mm});
            skCircle(sketch, "E2.16.22.0", {"center": v(425, 582.98) * mm, "radius": 3 * mm});
            skCircle(sketch, "E2.17.0.0", {"center": v(450, 32.98) * mm, "radius": 3 * mm});
            skCircle(sketch, "E2.17.1.0", {"center": v(450, 57.98) * mm, "radius": 3 * mm});
            skCircle(sketch, "E2.17.2.0", {"center": v(450, 82.98) * mm, "radius": 3 * mm});
            skCircle(sketch, "E2.17.3.0", {"center": v(450, 107.98) * mm, "radius": 3 * mm});
            skCircle(sketch, "E2.17.4.0", {"center": v(450, 132.98) * mm, "radius": 3 * mm});
            skCircle(sketch, "E2.17.5.0", {"center": v(450, 157.98) * mm, "radius": 3 * mm});
            skCircle(sketch, "E2.17.6.0", {"center": v(450, 182.98) * mm, "radius": 3 * mm});
            skCircle(sketch, "E2.17.7.0", {"center": v(450, 207.98) * mm, "radius": 3 * mm});
            skCircle(sketch, "E2.17.8.0", {"center": v(450, 232.98) * mm, "radius": 3 * mm});
            skCircle(sketch, "E2.17.9.0", {"center": v(450, 257.98) * mm, "radius": 3 * mm});
            skCircle(sketch, "E2.17.10.0", {"center": v(450, 282.98) * mm, "radius": 3 * mm});
            skCircle(sketch, "E2.17.11.0", {"center": v(450, 307.98) * mm, "radius": 3 * mm});
            skCircle(sketch, "E2.17.12.0", {"center": v(450, 332.98) * mm, "radius": 3 * mm});
            skCircle(sketch, "E2.17.13.0", {"center": v(450, 357.98) * mm, "radius": 3 * mm});
            skCircle(sketch, "E2.17.14.0", {"center": v(450, 382.98) * mm, "radius": 3 * mm});
            skCircle(sketch, "E2.17.15.0", {"center": v(450, 407.98) * mm, "radius": 3 * mm});
            skCircle(sketch, "E2.17.16.0", {"center": v(450, 432.98) * mm, "radius": 3 * mm});
            skCircle(sketch, "E2.17.17.0", {"center": v(450, 457.98) * mm, "radius": 3 * mm});
            skCircle(sketch, "E2.17.18.0", {"center": v(450, 482.98) * mm, "radius": 3 * mm});
            skCircle(sketch, "E2.17.19.0", {"center": v(450, 507.98) * mm, "radius": 3 * mm});
            skCircle(sketch, "E2.17.20.0", {"center": v(450, 532.98) * mm, "radius": 3 * mm});
            skCircle(sketch, "E2.17.21.0", {"center": v(450, 557.98) * mm, "radius": 3 * mm});
            skCircle(sketch, "E2.17.22.0", {"center": v(450, 582.98) * mm, "radius": 3 * mm});
            skCircle(sketch, "E2.18.0.0", {"center": v(475, 32.98) * mm, "radius": 3 * mm});
            skCircle(sketch, "E2.18.1.0", {"center": v(475, 57.98) * mm, "radius": 3 * mm});
            skCircle(sketch, "E2.18.2.0", {"center": v(475, 82.98) * mm, "radius": 3 * mm});
            skCircle(sketch, "E2.18.3.0", {"center": v(475, 107.98) * mm, "radius": 3 * mm});
            skCircle(sketch, "E2.18.4.0", {"center": v(475, 132.98) * mm, "radius": 3 * mm});
            skCircle(sketch, "E2.18.5.0", {"center": v(475, 157.98) * mm, "radius": 3 * mm});
            skCircle(sketch, "E2.18.6.0", {"center": v(475, 182.98) * mm, "radius": 3 * mm});
            skCircle(sketch, "E2.18.7.0", {"center": v(475, 207.98) * mm, "radius": 3 * mm});
            skCircle(sketch, "E2.18.8.0", {"center": v(475, 232.98) * mm, "radius": 3 * mm});
            skCircle(sketch, "E2.18.9.0", {"center": v(475, 257.98) * mm, "radius": 3 * mm});
            skCircle(sketch, "E2.18.10.0", {"center": v(475, 282.98) * mm, "radius": 3 * mm});
            skCircle(sketch, "E2.18.11.0", {"center": v(475, 307.98) * mm, "radius": 3 * mm});
            skCircle(sketch, "E2.18.12.0", {"center": v(475, 332.98) * mm, "radius": 3 * mm});
            skCircle(sketch, "E2.18.13.0", {"center": v(475, 357.98) * mm, "radius": 3 * mm});
            skCircle(sketch, "E2.18.14.0", {"center": v(475, 382.98) * mm, "radius": 3 * mm});
            skCircle(sketch, "E2.18.15.0", {"center": v(475, 407.98) * mm, "radius": 3 * mm});
            skCircle(sketch, "E2.18.16.0", {"center": v(475, 432.98) * mm, "radius": 3 * mm});
            skCircle(sketch, "E2.18.17.0", {"center": v(475, 457.98) * mm, "radius": 3 * mm});
            skCircle(sketch, "E2.18.18.0", {"center": v(475, 482.98) * mm, "radius": 3 * mm});
            skCircle(sketch, "E2.18.19.0", {"center": v(475, 507.98) * mm, "radius": 3 * mm});
            skCircle(sketch, "E2.18.20.0", {"center": v(475, 532.98) * mm, "radius": 3 * mm});
            skCircle(sketch, "E2.18.21.0", {"center": v(475, 557.98) * mm, "radius": 3 * mm});
            skCircle(sketch, "E2.18.22.0", {"center": v(475, 582.98) * mm, "radius": 3 * mm});
            skCircle(sketch, "E2.19.0.0", {"center": v(500, 32.98) * mm, "radius": 3 * mm});
            skCircle(sketch, "E2.19.1.0", {"center": v(500, 57.98) * mm, "radius": 3 * mm});
            skCircle(sketch, "E2.19.2.0", {"center": v(500, 82.98) * mm, "radius": 3 * mm});
            skCircle(sketch, "E2.19.3.0", {"center": v(500, 107.98) * mm, "radius": 3 * mm});
            skCircle(sketch, "E2.19.4.0", {"center": v(500, 132.98) * mm, "radius": 3 * mm});
            skCircle(sketch, "E2.19.5.0", {"center": v(500, 157.98) * mm, "radius": 3 * mm});
            skCircle(sketch, "E2.19.6.0", {"center": v(500, 182.98) * mm, "radius": 3 * mm});
            skCircle(sketch, "E2.19.7.0", {"center": v(500, 207.98) * mm, "radius": 3 * mm});
            skCircle(sketch, "E2.19.8.0", {"center": v(500, 232.98) * mm, "radius": 3 * mm});
            skCircle(sketch, "E2.19.9.0", {"center": v(500, 257.98) * mm, "radius": 3 * mm});
            skCircle(sketch, "E2.19.10.0", {"center": v(500, 282.98) * mm, "radius": 3 * mm});
            skCircle(sketch, "E2.19.11.0", {"center": v(500, 307.98) * mm, "radius": 3 * mm});
            skCircle(sketch, "E2.19.12.0", {"center": v(500, 332.98) * mm, "radius": 3 * mm});
            skCircle(sketch, "E2.19.13.0", {"center": v(500, 357.98) * mm, "radius": 3 * mm});
            skCircle(sketch, "E2.19.14.0", {"center": v(500, 382.98) * mm, "radius": 3 * mm});
            skCircle(sketch, "E2.19.15.0", {"center": v(500, 407.98) * mm, "radius": 3 * mm});
            skCircle(sketch, "E2.19.16.0", {"center": v(500, 432.98) * mm, "radius": 3 * mm});
            skCircle(sketch, "E2.19.17.0", {"center": v(500, 457.98) * mm, "radius": 3 * mm});
            skCircle(sketch, "E2.19.18.0", {"center": v(500, 482.98) * mm, "radius": 3 * mm});
            skCircle(sketch, "E2.19.19.0", {"center": v(500, 507.98) * mm, "radius": 3 * mm});
            skCircle(sketch, "E2.19.20.0", {"center": v(500, 532.98) * mm, "radius": 3 * mm});
            skCircle(sketch, "E2.19.21.0", {"center": v(500, 557.98) * mm, "radius": 3 * mm});
            skCircle(sketch, "E2.19.22.0", {"center": v(500, 582.98) * mm, "radius": 3 * mm});
            skCircle(sketch, "E2.20.0.0", {"center": v(525, 32.98) * mm, "radius": 3 * mm});
            skCircle(sketch, "E2.20.1.0", {"center": v(525, 57.98) * mm, "radius": 3 * mm});
            skCircle(sketch, "E2.20.2.0", {"center": v(525, 82.98) * mm, "radius": 3 * mm});
            skCircle(sketch, "E2.20.3.0", {"center": v(525, 107.98) * mm, "radius": 3 * mm});
            skCircle(sketch, "E2.20.4.0", {"center": v(525, 132.98) * mm, "radius": 3 * mm});
            skCircle(sketch, "E2.20.5.0", {"center": v(525, 157.98) * mm, "radius": 3 * mm});
            skCircle(sketch, "E2.20.6.0", {"center": v(525, 182.98) * mm, "radius": 3 * mm});
            skCircle(sketch, "E2.20.7.0", {"center": v(525, 207.98) * mm, "radius": 3 * mm});
            skCircle(sketch, "E2.20.8.0", {"center": v(525, 232.98) * mm, "radius": 3 * mm});
            skCircle(sketch, "E2.20.9.0", {"center": v(525, 257.98) * mm, "radius": 3 * mm});
            skCircle(sketch, "E2.20.10.0", {"center": v(525, 282.98) * mm, "radius": 3 * mm});
            skCircle(sketch, "E2.20.11.0", {"center": v(525, 307.98) * mm, "radius": 3 * mm});
            skCircle(sketch, "E2.20.12.0", {"center": v(525, 332.98) * mm, "radius": 3 * mm});
            skCircle(sketch, "E2.20.13.0", {"center": v(525, 357.98) * mm, "radius": 3 * mm});
            skCircle(sketch, "E2.20.14.0", {"center": v(525, 382.98) * mm, "radius": 3 * mm});
            skCircle(sketch, "E2.20.15.0", {"center": v(525, 407.98) * mm, "radius": 3 * mm});
            skCircle(sketch, "E2.20.16.0", {"center": v(525, 432.98) * mm, "radius": 3 * mm});
            skCircle(sketch, "E2.20.17.0", {"center": v(525, 457.98) * mm, "radius": 3 * mm});
            skCircle(sketch, "E2.20.18.0", {"center": v(525, 482.98) * mm, "radius": 3 * mm});
            skCircle(sketch, "E2.20.19.0", {"center": v(525, 507.98) * mm, "radius": 3 * mm});
            skCircle(sketch, "E2.20.20.0", {"center": v(525, 532.98) * mm, "radius": 3 * mm});
            skCircle(sketch, "E2.20.21.0", {"center": v(525, 557.98) * mm, "radius": 3 * mm});
            skCircle(sketch, "E2.20.22.0", {"center": v(525, 582.98) * mm, "radius": 3 * mm});
            skCircle(sketch, "E2.21.0.0", {"center": v(550, 32.98) * mm, "radius": 3 * mm});
            skCircle(sketch, "E2.21.1.0", {"center": v(550, 57.98) * mm, "radius": 3 * mm});
            skCircle(sketch, "E2.21.2.0", {"center": v(550, 82.98) * mm, "radius": 3 * mm});
            skCircle(sketch, "E2.21.3.0", {"center": v(550, 107.98) * mm, "radius": 3 * mm});
            skCircle(sketch, "E2.21.4.0", {"center": v(550, 132.98) * mm, "radius": 3 * mm});
            skCircle(sketch, "E2.21.5.0", {"center": v(550, 157.98) * mm, "radius": 3 * mm});
            skCircle(sketch, "E2.21.6.0", {"center": v(550, 182.98) * mm, "radius": 3 * mm});
            skCircle(sketch, "E2.21.7.0", {"center": v(550, 207.98) * mm, "radius": 3 * mm});
            skCircle(sketch, "E2.21.8.0", {"center": v(550, 232.98) * mm, "radius": 3 * mm});
            skCircle(sketch, "E2.21.9.0", {"center": v(550, 257.98) * mm, "radius": 3 * mm});
            skCircle(sketch, "E2.21.10.0", {"center": v(550, 282.98) * mm, "radius": 3 * mm});
            skCircle(sketch, "E2.21.11.0", {"center": v(550, 307.98) * mm, "radius": 3 * mm});
            skCircle(sketch, "E2.21.12.0", {"center": v(550, 332.98) * mm, "radius": 3 * mm});
            skCircle(sketch, "E2.21.13.0", {"center": v(550, 357.98) * mm, "radius": 3 * mm});
            skCircle(sketch, "E2.21.14.0", {"center": v(550, 382.98) * mm, "radius": 3 * mm});
            skCircle(sketch, "E2.21.15.0", {"center": v(550, 407.98) * mm, "radius": 3 * mm});
            skCircle(sketch, "E2.21.16.0", {"center": v(550, 432.98) * mm, "radius": 3 * mm});
            skCircle(sketch, "E2.21.17.0", {"center": v(550, 457.98) * mm, "radius": 3 * mm});
            skCircle(sketch, "E2.21.18.0", {"center": v(550, 482.98) * mm, "radius": 3 * mm});
            skCircle(sketch, "E2.21.19.0", {"center": v(550, 507.98) * mm, "radius": 3 * mm});
            skCircle(sketch, "E2.21.20.0", {"center": v(550, 532.98) * mm, "radius": 3 * mm});
            skCircle(sketch, "E2.21.21.0", {"center": v(550, 557.98) * mm, "radius": 3 * mm});
            skCircle(sketch, "E2.21.22.0", {"center": v(550, 582.98) * mm, "radius": 3 * mm});
            skCircle(sketch, "E2.22.0.0", {"center": v(575, 32.98) * mm, "radius": 3 * mm});
            skCircle(sketch, "E2.22.1.0", {"center": v(575, 57.98) * mm, "radius": 3 * mm});
            skCircle(sketch, "E2.22.2.0", {"center": v(575, 82.98) * mm, "radius": 3 * mm});
            skCircle(sketch, "E2.22.3.0", {"center": v(575, 107.98) * mm, "radius": 3 * mm});
            skCircle(sketch, "E2.22.4.0", {"center": v(575, 132.98) * mm, "radius": 3 * mm});
            skCircle(sketch, "E2.22.5.0", {"center": v(575, 157.98) * mm, "radius": 3 * mm});
            skCircle(sketch, "E2.22.6.0", {"center": v(575, 182.98) * mm, "radius": 3 * mm});
            skCircle(sketch, "E2.22.7.0", {"center": v(575, 207.98) * mm, "radius": 3 * mm});
            skCircle(sketch, "E2.22.8.0", {"center": v(575, 232.98) * mm, "radius": 3 * mm});
            skCircle(sketch, "E2.22.9.0", {"center": v(575, 257.98) * mm, "radius": 3 * mm});
            skCircle(sketch, "E2.22.10.0", {"center": v(575, 282.98) * mm, "radius": 3 * mm});
            skCircle(sketch, "E2.22.11.0", {"center": v(575, 307.98) * mm, "radius": 3 * mm});
            skCircle(sketch, "E2.22.12.0", {"center": v(575, 332.98) * mm, "radius": 3 * mm});
            skCircle(sketch, "E2.22.13.0", {"center": v(575, 357.98) * mm, "radius": 3 * mm});
            skCircle(sketch, "E2.22.14.0", {"center": v(575, 382.98) * mm, "radius": 3 * mm});
            skCircle(sketch, "E2.22.15.0", {"center": v(575, 407.98) * mm, "radius": 3 * mm});
            skCircle(sketch, "E2.22.16.0", {"center": v(575, 432.98) * mm, "radius": 3 * mm});
            skCircle(sketch, "E2.22.17.0", {"center": v(575, 457.98) * mm, "radius": 3 * mm});
            skCircle(sketch, "E2.22.18.0", {"center": v(575, 482.98) * mm, "radius": 3 * mm});
            skCircle(sketch, "E2.22.19.0", {"center": v(575, 507.98) * mm, "radius": 3 * mm});
            skCircle(sketch, "E2.22.20.0", {"center": v(575, 532.98) * mm, "radius": 3 * mm});
            skCircle(sketch, "E2.22.21.0", {"center": v(575, 557.98) * mm, "radius": 3 * mm});
            skCircle(sketch, "E2.22.22.0", {"center": v(575, 582.98) * mm, "radius": 3 * mm});
            skCircle(sketch, "E2.23.0.0", {"center": v(600, 32.98) * mm, "radius": 3 * mm});
            skCircle(sketch, "E2.23.1.0", {"center": v(600, 57.98) * mm, "radius": 3 * mm});
            skCircle(sketch, "E2.23.2.0", {"center": v(600, 82.98) * mm, "radius": 3 * mm});
            skCircle(sketch, "E2.23.3.0", {"center": v(600, 107.98) * mm, "radius": 3 * mm});
            skCircle(sketch, "E2.23.4.0", {"center": v(600, 132.98) * mm, "radius": 3 * mm});
            skCircle(sketch, "E2.23.5.0", {"center": v(600, 157.98) * mm, "radius": 3 * mm});
            skCircle(sketch, "E2.23.6.0", {"center": v(600, 182.98) * mm, "radius": 3 * mm});
            skCircle(sketch, "E2.23.7.0", {"center": v(600, 207.98) * mm, "radius": 3 * mm});
            skCircle(sketch, "E2.23.8.0", {"center": v(600, 232.98) * mm, "radius": 3 * mm});
            skCircle(sketch, "E2.23.9.0", {"center": v(600, 257.98) * mm, "radius": 3 * mm});
            skCircle(sketch, "E2.23.10.0", {"center": v(600, 282.98) * mm, "radius": 3 * mm});
            skCircle(sketch, "E2.23.11.0", {"center": v(600, 307.98) * mm, "radius": 3 * mm});
            skCircle(sketch, "E2.23.12.0", {"center": v(600, 332.98) * mm, "radius": 3 * mm});
            skCircle(sketch, "E2.23.13.0", {"center": v(600, 357.98) * mm, "radius": 3 * mm});
            skCircle(sketch, "E2.23.14.0", {"center": v(600, 382.98) * mm, "radius": 3 * mm});
            skCircle(sketch, "E2.23.15.0", {"center": v(600, 407.98) * mm, "radius": 3 * mm});
            skCircle(sketch, "E2.23.16.0", {"center": v(600, 432.98) * mm, "radius": 3 * mm});
            skCircle(sketch, "E2.23.17.0", {"center": v(600, 457.98) * mm, "radius": 3 * mm});
            skCircle(sketch, "E2.23.18.0", {"center": v(600, 482.98) * mm, "radius": 3 * mm});
            skCircle(sketch, "E2.23.19.0", {"center": v(600, 507.98) * mm, "radius": 3 * mm});
            skCircle(sketch, "E2.23.20.0", {"center": v(600, 532.98) * mm, "radius": 3 * mm});
            skCircle(sketch, "E2.23.21.0", {"center": v(600, 557.98) * mm, "radius": 3 * mm});
            skCircle(sketch, "E2.23.22.0", {"center": v(600, 582.98) * mm, "radius": 3 * mm});
            skCircle(sketch, "E2.24.0.0", {"center": v(625, 32.98) * mm, "radius": 3 * mm});
            skCircle(sketch, "E2.24.1.0", {"center": v(625, 57.98) * mm, "radius": 3 * mm});
            skCircle(sketch, "E2.24.2.0", {"center": v(625, 82.98) * mm, "radius": 3 * mm});
            skCircle(sketch, "E2.24.3.0", {"center": v(625, 107.98) * mm, "radius": 3 * mm});
            skCircle(sketch, "E2.24.4.0", {"center": v(625, 132.98) * mm, "radius": 3 * mm});
            skCircle(sketch, "E2.24.5.0", {"center": v(625, 157.98) * mm, "radius": 3 * mm});
            skCircle(sketch, "E2.24.6.0", {"center": v(625, 182.98) * mm, "radius": 3 * mm});
            skCircle(sketch, "E2.24.7.0", {"center": v(625, 207.98) * mm, "radius": 3 * mm});
            skCircle(sketch, "E2.24.8.0", {"center": v(625, 232.98) * mm, "radius": 3 * mm});
            skCircle(sketch, "E2.24.9.0", {"center": v(625, 257.98) * mm, "radius": 3 * mm});
            skCircle(sketch, "E2.24.10.0", {"center": v(625, 282.98) * mm, "radius": 3 * mm});
            skCircle(sketch, "E2.24.11.0", {"center": v(625, 307.98) * mm, "radius": 3 * mm});
            skCircle(sketch, "E2.24.12.0", {"center": v(625, 332.98) * mm, "radius": 3 * mm});
            skCircle(sketch, "E2.24.13.0", {"center": v(625, 357.98) * mm, "radius": 3 * mm});
            skCircle(sketch, "E2.24.14.0", {"center": v(625, 382.98) * mm, "radius": 3 * mm});
            skCircle(sketch, "E2.24.15.0", {"center": v(625, 407.98) * mm, "radius": 3 * mm});
            skCircle(sketch, "E2.24.16.0", {"center": v(625, 432.98) * mm, "radius": 3 * mm});
            skCircle(sketch, "E2.24.17.0", {"center": v(625, 457.98) * mm, "radius": 3 * mm});
            skCircle(sketch, "E2.24.18.0", {"center": v(625, 482.98) * mm, "radius": 3 * mm});
            skCircle(sketch, "E2.24.19.0", {"center": v(625, 507.98) * mm, "radius": 3 * mm});
            skCircle(sketch, "E2.24.20.0", {"center": v(625, 532.98) * mm, "radius": 3 * mm});
            skCircle(sketch, "E2.24.21.0", {"center": v(625, 557.98) * mm, "radius": 3 * mm});
            skCircle(sketch, "E2.24.22.0", {"center": v(625, 582.98) * mm, "radius": 3 * mm});
            skCircle(sketch, "E2.25.0.0", {"center": v(650, 32.98) * mm, "radius": 3 * mm});
            skCircle(sketch, "E2.25.1.0", {"center": v(650, 57.98) * mm, "radius": 3 * mm});
            skCircle(sketch, "E2.25.2.0", {"center": v(650, 82.98) * mm, "radius": 3 * mm});
            skCircle(sketch, "E2.25.3.0", {"center": v(650, 107.98) * mm, "radius": 3 * mm});
            skCircle(sketch, "E2.25.4.0", {"center": v(650, 132.98) * mm, "radius": 3 * mm});
            skCircle(sketch, "E2.25.5.0", {"center": v(650, 157.98) * mm, "radius": 3 * mm});
            skCircle(sketch, "E2.25.6.0", {"center": v(650, 182.98) * mm, "radius": 3 * mm});
            skCircle(sketch, "E2.25.7.0", {"center": v(650, 207.98) * mm, "radius": 3 * mm});
            skCircle(sketch, "E2.25.8.0", {"center": v(650, 232.98) * mm, "radius": 3 * mm});
            skCircle(sketch, "E2.25.9.0", {"center": v(650, 257.98) * mm, "radius": 3 * mm});
            skCircle(sketch, "E2.25.10.0", {"center": v(650, 282.98) * mm, "radius": 3 * mm});
            skCircle(sketch, "E2.25.11.0", {"center": v(650, 307.98) * mm, "radius": 3 * mm});
            skCircle(sketch, "E2.25.12.0", {"center": v(650, 332.98) * mm, "radius": 3 * mm});
            skCircle(sketch, "E2.25.13.0", {"center": v(650, 357.98) * mm, "radius": 3 * mm});
            skCircle(sketch, "E2.25.14.0", {"center": v(650, 382.98) * mm, "radius": 3 * mm});
            skCircle(sketch, "E2.25.15.0", {"center": v(650, 407.98) * mm, "radius": 3 * mm});
            skCircle(sketch, "E2.25.16.0", {"center": v(650, 432.98) * mm, "radius": 3 * mm});
            skCircle(sketch, "E2.25.17.0", {"center": v(650, 457.98) * mm, "radius": 3 * mm});
            skCircle(sketch, "E2.25.18.0", {"center": v(650, 482.98) * mm, "radius": 3 * mm});
            skCircle(sketch, "E2.25.19.0", {"center": v(650, 507.98) * mm, "radius": 3 * mm});
            skCircle(sketch, "E2.25.20.0", {"center": v(650, 532.98) * mm, "radius": 3 * mm});
            skCircle(sketch, "E2.25.21.0", {"center": v(650, 557.98) * mm, "radius": 3 * mm});
            skCircle(sketch, "E2.25.22.0", {"center": v(650, 582.98) * mm, "radius": 3 * mm});
            skCircle(sketch, "E2.26.0.0", {"center": v(675, 32.98) * mm, "radius": 3 * mm});
            skCircle(sketch, "E2.26.1.0", {"center": v(675, 57.98) * mm, "radius": 3 * mm});
            skCircle(sketch, "E2.26.2.0", {"center": v(675, 82.98) * mm, "radius": 3 * mm});
            skCircle(sketch, "E2.26.3.0", {"center": v(675, 107.98) * mm, "radius": 3 * mm});
            skCircle(sketch, "E2.26.4.0", {"center": v(675, 132.98) * mm, "radius": 3 * mm});
            skCircle(sketch, "E2.26.5.0", {"center": v(675, 157.98) * mm, "radius": 3 * mm});
            skCircle(sketch, "E2.26.6.0", {"center": v(675, 182.98) * mm, "radius": 3 * mm});
            skCircle(sketch, "E2.26.7.0", {"center": v(675, 207.98) * mm, "radius": 3 * mm});
            skCircle(sketch, "E2.26.8.0", {"center": v(675, 232.98) * mm, "radius": 3 * mm});
            skCircle(sketch, "E2.26.9.0", {"center": v(675, 257.98) * mm, "radius": 3 * mm});
            skCircle(sketch, "E2.26.10.0", {"center": v(675, 282.98) * mm, "radius": 3 * mm});
            skCircle(sketch, "E2.26.11.0", {"center": v(675, 307.98) * mm, "radius": 3 * mm});
            skCircle(sketch, "E2.26.12.0", {"center": v(675, 332.98) * mm, "radius": 3 * mm});
            skCircle(sketch, "E2.26.13.0", {"center": v(675, 357.98) * mm, "radius": 3 * mm});
            skCircle(sketch, "E2.26.14.0", {"center": v(675, 382.98) * mm, "radius": 3 * mm});
            skCircle(sketch, "E2.26.15.0", {"center": v(675, 407.98) * mm, "radius": 3 * mm});
            skCircle(sketch, "E2.26.16.0", {"center": v(675, 432.98) * mm, "radius": 3 * mm});
            skCircle(sketch, "E2.26.17.0", {"center": v(675, 457.98) * mm, "radius": 3 * mm});
            skCircle(sketch, "E2.26.18.0", {"center": v(675, 482.98) * mm, "radius": 3 * mm});
            skCircle(sketch, "E2.26.19.0", {"center": v(675, 507.98) * mm, "radius": 3 * mm});
            skCircle(sketch, "E2.26.20.0", {"center": v(675, 532.98) * mm, "radius": 3 * mm});
            skCircle(sketch, "E2.26.21.0", {"center": v(675, 557.98) * mm, "radius": 3 * mm});
            skCircle(sketch, "E2.26.22.0", {"center": v(675, 582.98) * mm, "radius": 3 * mm});
            skCircle(sketch, "E2.27.0.0", {"center": v(700, 32.98) * mm, "radius": 3 * mm});
            skCircle(sketch, "E2.27.1.0", {"center": v(700, 57.98) * mm, "radius": 3 * mm});
            skCircle(sketch, "E2.27.2.0", {"center": v(700, 82.98) * mm, "radius": 3 * mm});
            skCircle(sketch, "E2.27.3.0", {"center": v(700, 107.98) * mm, "radius": 3 * mm});
            skCircle(sketch, "E2.27.4.0", {"center": v(700, 132.98) * mm, "radius": 3 * mm});
            skCircle(sketch, "E2.27.5.0", {"center": v(700, 157.98) * mm, "radius": 3 * mm});
            skCircle(sketch, "E2.27.6.0", {"center": v(700, 182.98) * mm, "radius": 3 * mm});
            skCircle(sketch, "E2.27.7.0", {"center": v(700, 207.98) * mm, "radius": 3 * mm});
            skCircle(sketch, "E2.27.8.0", {"center": v(700, 232.98) * mm, "radius": 3 * mm});
            skCircle(sketch, "E2.27.9.0", {"center": v(700, 257.98) * mm, "radius": 3 * mm});
            skCircle(sketch, "E2.27.10.0", {"center": v(700, 282.98) * mm, "radius": 3 * mm});
            skCircle(sketch, "E2.27.11.0", {"center": v(700, 307.98) * mm, "radius": 3 * mm});
            skCircle(sketch, "E2.27.12.0", {"center": v(700, 332.98) * mm, "radius": 3 * mm});
            skCircle(sketch, "E2.27.13.0", {"center": v(700, 357.98) * mm, "radius": 3 * mm});
            skCircle(sketch, "E2.27.14.0", {"center": v(700, 382.98) * mm, "radius": 3 * mm});
            skCircle(sketch, "E2.27.15.0", {"center": v(700, 407.98) * mm, "radius": 3 * mm});
            skCircle(sketch, "E2.27.16.0", {"center": v(700, 432.98) * mm, "radius": 3 * mm});
            skCircle(sketch, "E2.27.17.0", {"center": v(700, 457.98) * mm, "radius": 3 * mm});
            skCircle(sketch, "E2.27.18.0", {"center": v(700, 482.98) * mm, "radius": 3 * mm});
            skCircle(sketch, "E2.27.19.0", {"center": v(700, 507.98) * mm, "radius": 3 * mm});
            skCircle(sketch, "E2.27.20.0", {"center": v(700, 532.98) * mm, "radius": 3 * mm});
            skCircle(sketch, "E2.27.21.0", {"center": v(700, 557.98) * mm, "radius": 3 * mm});
            skCircle(sketch, "E2.27.22.0", {"center": v(700, 582.98) * mm, "radius": 3 * mm});
            skCircle(sketch, "E2.28.0.0", {"center": v(725, 32.98) * mm, "radius": 3 * mm});
            skCircle(sketch, "E2.28.1.0", {"center": v(725, 57.98) * mm, "radius": 3 * mm});
            skCircle(sketch, "E2.28.2.0", {"center": v(725, 82.98) * mm, "radius": 3 * mm});
            skCircle(sketch, "E2.28.3.0", {"center": v(725, 107.98) * mm, "radius": 3 * mm});
            skCircle(sketch, "E2.28.4.0", {"center": v(725, 132.98) * mm, "radius": 3 * mm});
            skCircle(sketch, "E2.28.5.0", {"center": v(725, 157.98) * mm, "radius": 3 * mm});
            skCircle(sketch, "E2.28.6.0", {"center": v(725, 182.98) * mm, "radius": 3 * mm});
            skCircle(sketch, "E2.28.7.0", {"center": v(725, 207.98) * mm, "radius": 3 * mm});
            skCircle(sketch, "E2.28.8.0", {"center": v(725, 232.98) * mm, "radius": 3 * mm});
            skCircle(sketch, "E2.28.9.0", {"center": v(725, 257.98) * mm, "radius": 3 * mm});
            skCircle(sketch, "E2.28.10.0", {"center": v(725, 282.98) * mm, "radius": 3 * mm});
            skCircle(sketch, "E2.28.11.0", {"center": v(725, 307.98) * mm, "radius": 3 * mm});
            skCircle(sketch, "E2.28.12.0", {"center": v(725, 332.98) * mm, "radius": 3 * mm});
            skCircle(sketch, "E2.28.13.0", {"center": v(725, 357.98) * mm, "radius": 3 * mm});
            skCircle(sketch, "E2.28.14.0", {"center": v(725, 382.98) * mm, "radius": 3 * mm});
            skCircle(sketch, "E2.28.15.0", {"center": v(725, 407.98) * mm, "radius": 3 * mm});
            skCircle(sketch, "E2.28.16.0", {"center": v(725, 432.98) * mm, "radius": 3 * mm});
            skCircle(sketch, "E2.28.17.0", {"center": v(725, 457.98) * mm, "radius": 3 * mm});
            skCircle(sketch, "E2.28.18.0", {"center": v(725, 482.98) * mm, "radius": 3 * mm});
            skCircle(sketch, "E2.28.19.0", {"center": v(725, 507.98) * mm, "radius": 3 * mm});
            skCircle(sketch, "E2.28.20.0", {"center": v(725, 532.98) * mm, "radius": 3 * mm});
            skCircle(sketch, "E2.28.21.0", {"center": v(725, 557.98) * mm, "radius": 3 * mm});
            skCircle(sketch, "E2.28.22.0", {"center": v(725, 582.98) * mm, "radius": 3 * mm});
            skCircle(sketch, "E2.29.0.0", {"center": v(750, 32.98) * mm, "radius": 3 * mm});
            skCircle(sketch, "E2.29.1.0", {"center": v(750, 57.98) * mm, "radius": 3 * mm});
            skCircle(sketch, "E2.29.2.0", {"center": v(750, 82.98) * mm, "radius": 3 * mm});
            skCircle(sketch, "E2.29.3.0", {"center": v(750, 107.98) * mm, "radius": 3 * mm});
            skCircle(sketch, "E2.29.4.0", {"center": v(750, 132.98) * mm, "radius": 3 * mm});
            skCircle(sketch, "E2.29.5.0", {"center": v(750, 157.98) * mm, "radius": 3 * mm});
            skCircle(sketch, "E2.29.6.0", {"center": v(750, 182.98) * mm, "radius": 3 * mm});
            skCircle(sketch, "E2.29.7.0", {"center": v(750, 207.98) * mm, "radius": 3 * mm});
            skCircle(sketch, "E2.29.8.0", {"center": v(750, 232.98) * mm, "radius": 3 * mm});
            skCircle(sketch, "E2.29.9.0", {"center": v(750, 257.98) * mm, "radius": 3 * mm});
            skCircle(sketch, "E2.29.10.0", {"center": v(750, 282.98) * mm, "radius": 3 * mm});
            skCircle(sketch, "E2.29.11.0", {"center": v(750, 307.98) * mm, "radius": 3 * mm});
            skCircle(sketch, "E2.29.12.0", {"center": v(750, 332.98) * mm, "radius": 3 * mm});
            skCircle(sketch, "E2.29.13.0", {"center": v(750, 357.98) * mm, "radius": 3 * mm});
            skCircle(sketch, "E2.29.14.0", {"center": v(750, 382.98) * mm, "radius": 3 * mm});
            skCircle(sketch, "E2.29.15.0", {"center": v(750, 407.98) * mm, "radius": 3 * mm});
            skCircle(sketch, "E2.29.16.0", {"center": v(750, 432.98) * mm, "radius": 3 * mm});
            skCircle(sketch, "E2.29.17.0", {"center": v(750, 457.98) * mm, "radius": 3 * mm});
            skCircle(sketch, "E2.29.18.0", {"center": v(750, 482.98) * mm, "radius": 3 * mm});
            skCircle(sketch, "E2.29.19.0", {"center": v(750, 507.98) * mm, "radius": 3 * mm});
            skCircle(sketch, "E2.29.20.0", {"center": v(750, 532.98) * mm, "radius": 3 * mm});
            skCircle(sketch, "E2.29.21.0", {"center": v(750, 557.98) * mm, "radius": 3 * mm});
            skCircle(sketch, "E2.29.22.0", {"center": v(750, 582.98) * mm, "radius": 3 * mm});
            skCircle(sketch, "E2.30.0.0", {"center": v(775, 32.98) * mm, "radius": 3 * mm});
            skCircle(sketch, "E2.30.1.0", {"center": v(775, 57.98) * mm, "radius": 3 * mm});
            skCircle(sketch, "E2.30.2.0", {"center": v(775, 82.98) * mm, "radius": 3 * mm});
            skCircle(sketch, "E2.30.3.0", {"center": v(775, 107.98) * mm, "radius": 3 * mm});
            skCircle(sketch, "E2.30.4.0", {"center": v(775, 132.98) * mm, "radius": 3 * mm});
            skCircle(sketch, "E2.30.5.0", {"center": v(775, 157.98) * mm, "radius": 3 * mm});
            skCircle(sketch, "E2.30.6.0", {"center": v(775, 182.98) * mm, "radius": 3 * mm});
            skCircle(sketch, "E2.30.7.0", {"center": v(775, 207.98) * mm, "radius": 3 * mm});
            skCircle(sketch, "E2.30.8.0", {"center": v(775, 232.98) * mm, "radius": 3 * mm});
            skCircle(sketch, "E2.30.9.0", {"center": v(775, 257.98) * mm, "radius": 3 * mm});
            skCircle(sketch, "E2.30.10.0", {"center": v(775, 282.98) * mm, "radius": 3 * mm});
            skCircle(sketch, "E2.30.11.0", {"center": v(775, 307.98) * mm, "radius": 3 * mm});
            skCircle(sketch, "E2.30.12.0", {"center": v(775, 332.98) * mm, "radius": 3 * mm});
            skCircle(sketch, "E2.30.13.0", {"center": v(775, 357.98) * mm, "radius": 3 * mm});
            skCircle(sketch, "E2.30.14.0", {"center": v(775, 382.98) * mm, "radius": 3 * mm});
            skCircle(sketch, "E2.30.15.0", {"center": v(775, 407.98) * mm, "radius": 3 * mm});
            skCircle(sketch, "E2.30.16.0", {"center": v(775, 432.98) * mm, "radius": 3 * mm});
            skCircle(sketch, "E2.30.17.0", {"center": v(775, 457.98) * mm, "radius": 3 * mm});
            skCircle(sketch, "E2.30.18.0", {"center": v(775, 482.98) * mm, "radius": 3 * mm});
            skCircle(sketch, "E2.30.19.0", {"center": v(775, 507.98) * mm, "radius": 3 * mm});
            skCircle(sketch, "E2.30.20.0", {"center": v(775, 532.98) * mm, "radius": 3 * mm});
            skCircle(sketch, "E2.30.21.0", {"center": v(775, 557.98) * mm, "radius": 3 * mm});
            skCircle(sketch, "E2.30.22.0", {"center": v(775, 582.98) * mm, "radius": 3 * mm});
            skCircle(sketch, "E2.31.0.0", {"center": v(800, 32.98) * mm, "radius": 3 * mm});
            skCircle(sketch, "E2.31.1.0", {"center": v(800, 57.98) * mm, "radius": 3 * mm});
            skCircle(sketch, "E2.31.2.0", {"center": v(800, 82.98) * mm, "radius": 3 * mm});
            skCircle(sketch, "E2.31.3.0", {"center": v(800, 107.98) * mm, "radius": 3 * mm});
            skCircle(sketch, "E2.31.4.0", {"center": v(800, 132.98) * mm, "radius": 3 * mm});
            skCircle(sketch, "E2.31.5.0", {"center": v(800, 157.98) * mm, "radius": 3 * mm});
            skCircle(sketch, "E2.31.6.0", {"center": v(800, 182.98) * mm, "radius": 3 * mm});
            skCircle(sketch, "E2.31.7.0", {"center": v(800, 207.98) * mm, "radius": 3 * mm});
            skCircle(sketch, "E2.31.8.0", {"center": v(800, 232.98) * mm, "radius": 3 * mm});
            skCircle(sketch, "E2.31.9.0", {"center": v(800, 257.98) * mm, "radius": 3 * mm});
            skCircle(sketch, "E2.31.10.0", {"center": v(800, 282.98) * mm, "radius": 3 * mm});
            skCircle(sketch, "E2.31.11.0", {"center": v(800, 307.98) * mm, "radius": 3 * mm});
            skCircle(sketch, "E2.31.12.0", {"center": v(800, 332.98) * mm, "radius": 3 * mm});
            skCircle(sketch, "E2.31.13.0", {"center": v(800, 357.98) * mm, "radius": 3 * mm});
            skCircle(sketch, "E2.31.14.0", {"center": v(800, 382.98) * mm, "radius": 3 * mm});
            skCircle(sketch, "E2.31.15.0", {"center": v(800, 407.98) * mm, "radius": 3 * mm});
            skCircle(sketch, "E2.31.16.0", {"center": v(800, 432.98) * mm, "radius": 3 * mm});
            skCircle(sketch, "E2.31.17.0", {"center": v(800, 457.98) * mm, "radius": 3 * mm});
            skCircle(sketch, "E2.31.18.0", {"center": v(800, 482.98) * mm, "radius": 3 * mm});
            skCircle(sketch, "E2.31.19.0", {"center": v(800, 507.98) * mm, "radius": 3 * mm});
            skCircle(sketch, "E2.31.20.0", {"center": v(800, 532.98) * mm, "radius": 3 * mm});
            skCircle(sketch, "E2.31.21.0", {"center": v(800, 557.98) * mm, "radius": 3 * mm});
            skCircle(sketch, "E2.31.22.0", {"center": v(800, 582.98) * mm, "radius": 3 * mm});
            skCircle(sketch, "E2.32.0.0", {"center": v(825, 32.98) * mm, "radius": 3 * mm});
            skCircle(sketch, "E2.32.1.0", {"center": v(825, 57.98) * mm, "radius": 3 * mm});
            skCircle(sketch, "E2.32.2.0", {"center": v(825, 82.98) * mm, "radius": 3 * mm});
            skCircle(sketch, "E2.32.3.0", {"center": v(825, 107.98) * mm, "radius": 3 * mm});
            skCircle(sketch, "E2.32.4.0", {"center": v(825, 132.98) * mm, "radius": 3 * mm});
            skCircle(sketch, "E2.32.5.0", {"center": v(825, 157.98) * mm, "radius": 3 * mm});
            skCircle(sketch, "E2.32.6.0", {"center": v(825, 182.98) * mm, "radius": 3 * mm});
            skCircle(sketch, "E2.32.7.0", {"center": v(825, 207.98) * mm, "radius": 3 * mm});
            skCircle(sketch, "E2.32.8.0", {"center": v(825, 232.98) * mm, "radius": 3 * mm});
            skCircle(sketch, "E2.32.9.0", {"center": v(825, 257.98) * mm, "radius": 3 * mm});
            skCircle(sketch, "E2.32.10.0", {"center": v(825, 282.98) * mm, "radius": 3 * mm});
            skCircle(sketch, "E2.32.11.0", {"center": v(825, 307.98) * mm, "radius": 3 * mm});
            skCircle(sketch, "E2.32.12.0", {"center": v(825, 332.98) * mm, "radius": 3 * mm});
            skCircle(sketch, "E2.32.13.0", {"center": v(825, 357.98) * mm, "radius": 3 * mm});
            skCircle(sketch, "E2.32.14.0", {"center": v(825, 382.98) * mm, "radius": 3 * mm});
            skCircle(sketch, "E2.32.15.0", {"center": v(825, 407.98) * mm, "radius": 3 * mm});
            skCircle(sketch, "E2.32.16.0", {"center": v(825, 432.98) * mm, "radius": 3 * mm});
            skCircle(sketch, "E2.32.17.0", {"center": v(825, 457.98) * mm, "radius": 3 * mm});
            skCircle(sketch, "E2.32.18.0", {"center": v(825, 482.98) * mm, "radius": 3 * mm});
            skCircle(sketch, "E2.32.19.0", {"center": v(825, 507.98) * mm, "radius": 3 * mm});
            skCircle(sketch, "E2.32.20.0", {"center": v(825, 532.98) * mm, "radius": 3 * mm});
            skCircle(sketch, "E2.32.21.0", {"center": v(825, 557.98) * mm, "radius": 3 * mm});
            skCircle(sketch, "E2.32.22.0", {"center": v(825, 582.98) * mm, "radius": 3 * mm});
            skCircle(sketch, "E2.33.0.0", {"center": v(850, 32.98) * mm, "radius": 3 * mm});
            skCircle(sketch, "E2.33.1.0", {"center": v(850, 57.98) * mm, "radius": 3 * mm});
            skCircle(sketch, "E2.33.2.0", {"center": v(850, 82.98) * mm, "radius": 3 * mm});
            skCircle(sketch, "E2.33.3.0", {"center": v(850, 107.98) * mm, "radius": 3 * mm});
            skCircle(sketch, "E2.33.4.0", {"center": v(850, 132.98) * mm, "radius": 3 * mm});
            skCircle(sketch, "E2.33.5.0", {"center": v(850, 157.98) * mm, "radius": 3 * mm});
            skCircle(sketch, "E2.33.6.0", {"center": v(850, 182.98) * mm, "radius": 3 * mm});
            skCircle(sketch, "E2.33.7.0", {"center": v(850, 207.98) * mm, "radius": 3 * mm});
            skCircle(sketch, "E2.33.8.0", {"center": v(850, 232.98) * mm, "radius": 3 * mm});
            skCircle(sketch, "E2.33.9.0", {"center": v(850, 257.98) * mm, "radius": 3 * mm});
            skCircle(sketch, "E2.33.10.0", {"center": v(850, 282.98) * mm, "radius": 3 * mm});
            skCircle(sketch, "E2.33.11.0", {"center": v(850, 307.98) * mm, "radius": 3 * mm});
            skCircle(sketch, "E2.33.12.0", {"center": v(850, 332.98) * mm, "radius": 3 * mm});
            skCircle(sketch, "E2.33.13.0", {"center": v(850, 357.98) * mm, "radius": 3 * mm});
            skCircle(sketch, "E2.33.14.0", {"center": v(850, 382.98) * mm, "radius": 3 * mm});
            skCircle(sketch, "E2.33.15.0", {"center": v(850, 407.98) * mm, "radius": 3 * mm});
            skCircle(sketch, "E2.33.16.0", {"center": v(850, 432.98) * mm, "radius": 3 * mm});
            skCircle(sketch, "E2.33.17.0", {"center": v(850, 457.98) * mm, "radius": 3 * mm});
            skCircle(sketch, "E2.33.18.0", {"center": v(850, 482.98) * mm, "radius": 3 * mm});
            skCircle(sketch, "E2.33.19.0", {"center": v(850, 507.98) * mm, "radius": 3 * mm});
            skCircle(sketch, "E2.33.20.0", {"center": v(850, 532.98) * mm, "radius": 3 * mm});
            skCircle(sketch, "E2.33.21.0", {"center": v(850, 557.98) * mm, "radius": 3 * mm});
            skCircle(sketch, "E2.33.22.0", {"center": v(850, 582.98) * mm, "radius": 3 * mm});
            skCircle(sketch, "E2.34.0.0", {"center": v(875, 32.98) * mm, "radius": 3 * mm});
            skCircle(sketch, "E2.34.1.0", {"center": v(875, 57.98) * mm, "radius": 3 * mm});
            skCircle(sketch, "E2.34.2.0", {"center": v(875, 82.98) * mm, "radius": 3 * mm});
            skCircle(sketch, "E2.34.3.0", {"center": v(875, 107.98) * mm, "radius": 3 * mm});
            skCircle(sketch, "E2.34.4.0", {"center": v(875, 132.98) * mm, "radius": 3 * mm});
            skCircle(sketch, "E2.34.5.0", {"center": v(875, 157.98) * mm, "radius": 3 * mm});
            skCircle(sketch, "E2.34.6.0", {"center": v(875, 182.98) * mm, "radius": 3 * mm});
            skCircle(sketch, "E2.34.7.0", {"center": v(875, 207.98) * mm, "radius": 3 * mm});
            skCircle(sketch, "E2.34.8.0", {"center": v(875, 232.98) * mm, "radius": 3 * mm});
            skCircle(sketch, "E2.34.9.0", {"center": v(875, 257.98) * mm, "radius": 3 * mm});
            skCircle(sketch, "E2.34.10.0", {"center": v(875, 282.98) * mm, "radius": 3 * mm});
            skCircle(sketch, "E2.34.11.0", {"center": v(875, 307.98) * mm, "radius": 3 * mm});
            skCircle(sketch, "E2.34.12.0", {"center": v(875, 332.98) * mm, "radius": 3 * mm});
            skCircle(sketch, "E2.34.13.0", {"center": v(875, 357.98) * mm, "radius": 3 * mm});
            skCircle(sketch, "E2.34.14.0", {"center": v(875, 382.98) * mm, "radius": 3 * mm});
            skCircle(sketch, "E2.34.15.0", {"center": v(875, 407.98) * mm, "radius": 3 * mm});
            skCircle(sketch, "E2.34.16.0", {"center": v(875, 432.98) * mm, "radius": 3 * mm});
            skCircle(sketch, "E2.34.17.0", {"center": v(875, 457.98) * mm, "radius": 3 * mm});
            skCircle(sketch, "E2.34.18.0", {"center": v(875, 482.98) * mm, "radius": 3 * mm});
            skCircle(sketch, "E2.34.19.0", {"center": v(875, 507.98) * mm, "radius": 3 * mm});
            skCircle(sketch, "E2.34.20.0", {"center": v(875, 532.98) * mm, "radius": 3 * mm});
            skCircle(sketch, "E2.34.21.0", {"center": v(875, 557.98) * mm, "radius": 3 * mm});
            skCircle(sketch, "E2.34.22.0", {"center": v(875, 582.98) * mm, "radius": 3 * mm});
            skLineSegment(sketch, "E2.direction1", {"start": v(25, 32.98) * mm, "end": v(50, 32.98) * mm, "construction": true});
            skLineSegment(sketch, "E2.direction2", {"start": v(25, 32.98) * mm, "end": v(25, 57.98) * mm, "construction": true});
            skSolve(sketch);
        }
        {
            var Q0;
            Q0=qSketchRegion(id+"F2",true);
            extrude(context, id + "F3", {"entities" : qUnion([Q0]), "operationType" : NewBodyOperationType.REMOVE, "oppositeDirection" : true, "depth" : 10 * mm});
        }
        {
            var Q0;
            Q0=makeQuery(id+"F1.opExtrude","CAP_FACE",FACE,{"disambiguationData":[OSD([sQuery(id+"F0.wireOp",EDGE,"E0.bottom"),sQuery(id+"F0.wireOp",EDGE,"E0.top"),sQuery(id+"F0.wireOp",EDGE,"E0.left"),sQuery(id+"F0.wireOp",EDGE,"E0.right")])],"isStart":false});
            var sketch = newSketch(context, id + "F4", { "sketchPlane" : qUnion([Q0])});
            skLineSegment(sketch, "E3.bottom", {"start": v(600, 382.98) * mm, "end": v(650, 382.98) * mm});
            skLineSegment(sketch, "E3.top", {"start": v(600, 207.98) * mm, "end": v(650, 207.98) * mm});
            skLineSegment(sketch, "E3.left", {"start": v(600, 382.98) * mm, "end": v(600, 207.98) * mm});
            skLineSegment(sketch, "E3.right", {"start": v(650, 382.98) * mm, "end": v(650, 207.98) * mm});
            skSolve(sketch);
        }
        {
            var Q0;
            Q0=qSketchRegion(id+"F4",true);
            extrude(context, id + "F5", {"entities" : qUnion([Q0]), "depth" : 250 * mm});
        }
        {
            var Q0;
            Q0=makeQuery(id+"F5.opExtrude","SWEPT_FACE",FACE,{"disambiguationData":[OSD([sQuery(id+"F4.wireOp",EDGE,"E3.left")])]});
            var sketch = newSketch(context, id + "F6", { "sketchPlane" : qUnion([Q0])});
            skCircle(sketch, "E4", {"center": v(-295.48, 225) * mm, "radius": 20 * mm, "construction": true});
            skPoint(sketch, "E5", {"position": v(-295.48, 275) * mm});
            skCircle(sketch, "E6", {"center": v(-295.48, 225) * mm, "radius": 15 * mm, "construction": true});
            skCircle(sketch, "E7", {"center": v(-295.48, 240) * mm, "radius": 1.75 * mm});
            skLineSegment(sketch, "E8", {"start": v(-295.48, 225) * mm, "end": v(-295.48, 275) * mm, "construction": true});
            skCircle(sketch, "E9", {"center": v(-282.49, 217.5) * mm, "radius": 1.75 * mm});
            skCircle(sketch, "E10", {"center": v(-308.47, 217.5) * mm, "radius": 1.75 * mm});
            skLineSegment(sketch, "E11", {"start": v(-282.49, 217.5) * mm, "end": v(-295.48, 225) * mm, "construction": true});
            skLineSegment(sketch, "E12", {"start": v(-295.48, 225) * mm, "end": v(-308.47, 217.5) * mm, "construction": true});
            skSolve(sketch);
        }
        {
            var Q0;
            Q0=qSketchRegion(id+"F6",true);
            extrude(context, id + "F7", {"entities" : qUnion([Q0]), "operationType" : NewBodyOperationType.REMOVE, "endBound" : BoundingType.THROUGH_ALL, "oppositeDirection" : true, "depth" : 25 * mm});
        }
        {
            var Q0;
            Q0=makeQuery(id+"F5.opExtrude","SWEPT_FACE",FACE,{"disambiguationData":[OSD([sQuery(id+"F4.wireOp",EDGE,"E3.left")])]});
            var sketch = newSketch(context, id + "F8", { "sketchPlane" : qUnion([Q0])});
            skCircle(sketch, "E13", {"center": v(-295.48, 225) * mm, "radius": 20 * mm});
            skPoint(sketch, "E14", {"position": v(-295.48, 275) * mm});
            skSolve(sketch);
        }
        {
            var Q0;
            Q0=qSketchRegion(id+"F8",true);
            extrude(context, id + "F9", {"entities" : qUnion([Q0]), "depth" : 20 * mm});
        }
    });
